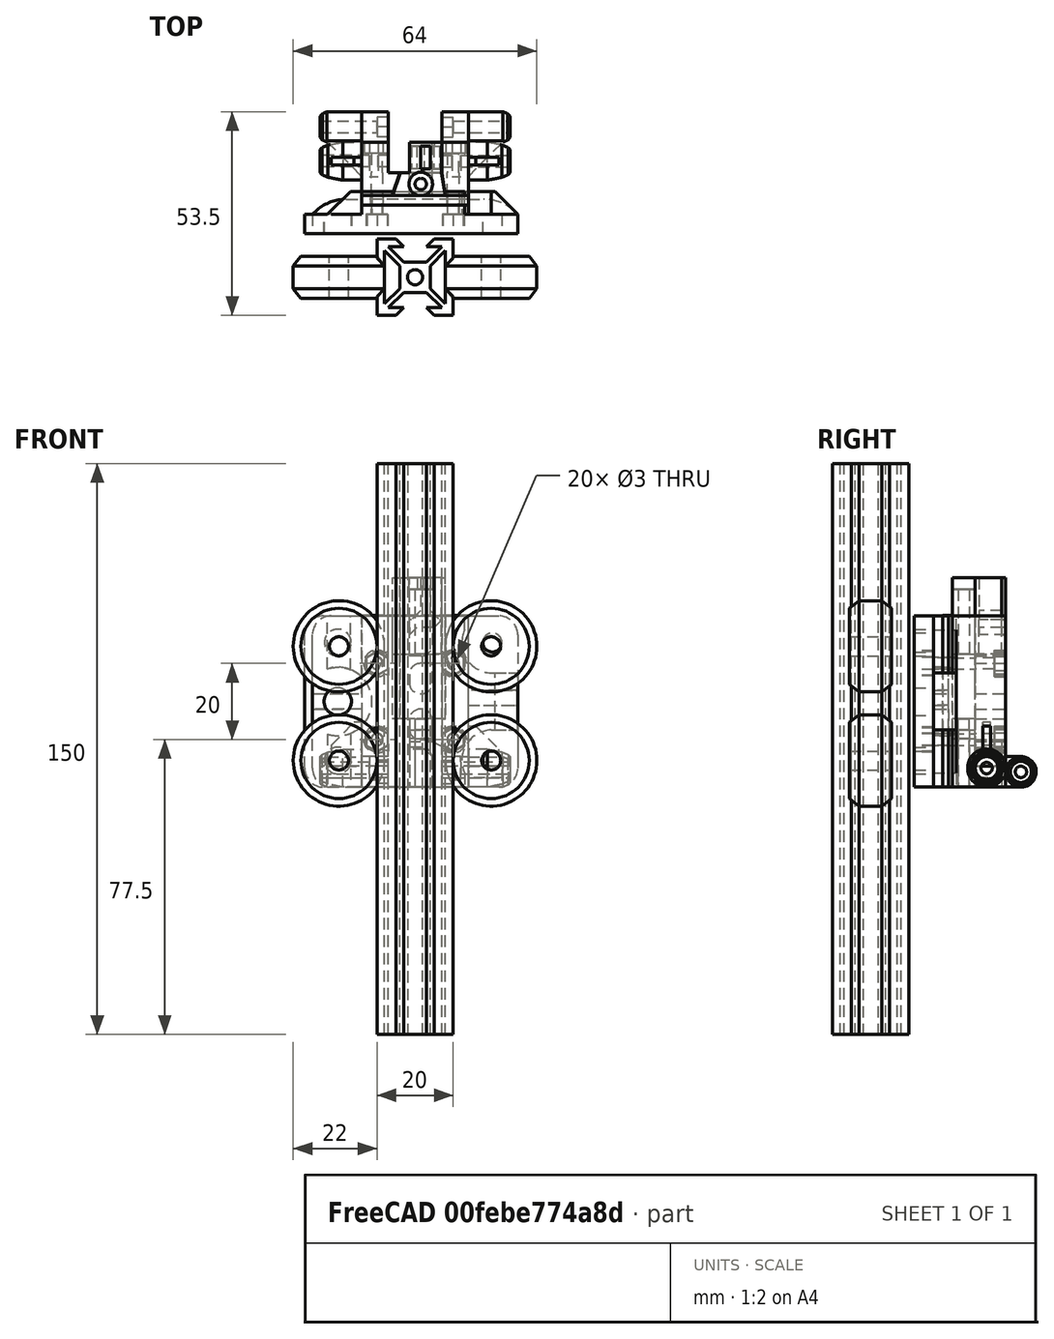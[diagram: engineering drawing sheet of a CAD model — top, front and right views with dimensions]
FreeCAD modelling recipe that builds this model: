
FCSTD DOCUMENT  (FreeCAD 0.18R16146 (Git))
Label: carriage
License: All rights reserved
LicenseURL: http://en.wikipedia.org/wiki/All_rights_reserved
objects: Sketcher::SketchObject×42, PartDesign::Pad×22, PartDesign::Pocket×16, PartDesign::Chamfer×13, PartDesign::Body×11, PartDesign::Fillet×5, PartDesign::Revolution×4, Mesh::Feature×3
note: 155 computed .brp shape members not serialized (recipe doc carries the construction recipe); baked Part::Feature solids carry a one-line shape summary decoded from their .brp

FEATURE [Sketcher::SketchObject] Sketch
  MapMode = 5
  Support = -> [XY_Plane]
  sketch-geometry (42):
    g0: LineSegment [constr] StartX=10 StartY=-10 StartZ=0 EndX=10 EndY=10 EndZ=0
    g1: LineSegment [constr] StartX=10 StartY=10 StartZ=0 EndX=-10 EndY=10 EndZ=0
    g2: LineSegment [constr] StartX=-10 StartY=10 StartZ=0 EndX=-10 EndY=-10 EndZ=0
    g3: LineSegment [constr] StartX=-10 StartY=-10 StartZ=0 EndX=10 EndY=-10 EndZ=0
    g4: Circle [constr] CenterX=0 CenterY=0 CenterZ=0 NormalX=0 NormalY=0 NormalZ=1 AngleXU=0 Radius=14.1421
    g5: Circle CenterX=0 CenterY=0 CenterZ=0 NormalX=0 NormalY=0 NormalZ=1 AngleXU=0 Radius=2
    g6: LineSegment StartX=-10 StartY=10 StartZ=0 EndX=-10 EndY=5 EndZ=0
    g7: LineSegment StartX=-10 StartY=10 StartZ=0 EndX=-5 EndY=10 EndZ=0
    g8: LineSegment StartX=10 StartY=10 StartZ=0 EndX=5 EndY=10 EndZ=0
    g9: LineSegment StartX=10 StartY=10 StartZ=0 EndX=10 EndY=5 EndZ=0
    g10: LineSegment StartX=10 StartY=-10 StartZ=0 EndX=10 EndY=-5 EndZ=0
    g11: LineSegment StartX=10 StartY=-10 StartZ=0 EndX=5 EndY=-10 EndZ=0
    g12: LineSegment StartX=-10 StartY=-10 StartZ=0 EndX=-5 EndY=-10 EndZ=0
    g13: LineSegment StartX=-10 StartY=-10 StartZ=0 EndX=-10 EndY=-5 EndZ=0
    g14: LineSegment StartX=-3 StartY=4 StartZ=0 EndX=3 EndY=4 EndZ=0
    g15: LineSegment StartX=4 StartY=3 StartZ=0 EndX=4 EndY=-3 EndZ=0
    g16: LineSegment StartX=-3 StartY=-4 StartZ=0 EndX=3 EndY=-4 EndZ=0
    g17: LineSegment StartX=-4 StartY=-3 StartZ=0 EndX=-4 EndY=3 EndZ=0
    g18: LineSegment StartX=-5 StartY=-10 StartZ=0 EndX=-3 EndY=-8 EndZ=0
    g19: LineSegment StartX=5 StartY=-10 StartZ=0 EndX=3 EndY=-8 EndZ=0
    g20: LineSegment StartX=-10 StartY=-5 StartZ=0 EndX=-8 EndY=-3 EndZ=0
    g21: LineSegment StartX=-10 StartY=5 StartZ=0 EndX=-8 EndY=3 EndZ=0
    g22: LineSegment StartX=-5 StartY=10 StartZ=0 EndX=-3.00001 EndY=7.99999 EndZ=0
    g23: LineSegment StartX=5 StartY=10 StartZ=0 EndX=2.99999 EndY=8.00001 EndZ=0
    g24: LineSegment StartX=10 StartY=-5 StartZ=0 EndX=7.99999 EndY=-3.00001 EndZ=0
    g25: LineSegment StartX=10 StartY=5 StartZ=0 EndX=8.00001 EndY=2.99999 EndZ=0
    g26: LineSegment StartX=-4 StartY=-3 StartZ=0 EndX=-8 EndY=-7 EndZ=0
    g27: LineSegment StartX=-3 StartY=-4 StartZ=0 EndX=-7 EndY=-8 EndZ=0
    g28: LineSegment StartX=3 StartY=-4 StartZ=0 EndX=6.99999 EndY=-8 EndZ=0
    g29: LineSegment StartX=4 StartY=-3 StartZ=0 EndX=7.99999 EndY=-7 EndZ=0
    g30: LineSegment StartX=-4 StartY=3 StartZ=0 EndX=-8 EndY=6.99999 EndZ=0
    g31: LineSegment StartX=-3 StartY=4 StartZ=0 EndX=-7 EndY=7.99999 EndZ=0
    g32: LineSegment StartX=3 StartY=4 StartZ=0 EndX=6.99998 EndY=8.00001 EndZ=0
    g33: LineSegment StartX=4 StartY=3 StartZ=0 EndX=8.00001 EndY=6.99999 EndZ=0
    g34: LineSegment StartX=-8 StartY=3 StartZ=0 EndX=-8 EndY=6.99999 EndZ=0
    g35: LineSegment StartX=-7 StartY=7.99999 StartZ=0 EndX=-3.00001 EndY=7.99999 EndZ=0
    g36: LineSegment StartX=2.99999 StartY=8.00001 StartZ=0 EndX=6.99998 EndY=8.00001 EndZ=0
    g37: LineSegment StartX=8.00001 StartY=6.99999 StartZ=0 EndX=8.00001 EndY=2.99999 EndZ=0
    g38: LineSegment StartX=7.99999 StartY=-7 StartZ=0 EndX=7.99999 EndY=-3.00001 EndZ=0
    g39: LineSegment StartX=3 StartY=-8 StartZ=0 EndX=6.99999 EndY=-8 EndZ=0
    g40: LineSegment StartX=-7 StartY=-8 StartZ=0 EndX=-3 EndY=-8 EndZ=0
    g41: LineSegment StartX=-8 StartY=-7 StartZ=0 EndX=-8 EndY=-3 EndZ=0
  constraints (118):
    c: Coincident(g0,g1)
    c: Coincident(g1,g2)
    c: Coincident(g2,g3)
    c: Coincident(g3,g0)
    c: Equal(g0,g1)
    c: Equal(g0,g2)
    c: Equal(g0,g3)
    c: PointOnObject(g0,g4)
    c: PointOnObject(g1,g4)
    c: PointOnObject(g2,g4)
    c: PointOnObject(g3,g4)
    c: Coincident(g4,g-1)
    c: DistanceX(g3,g3) = 20
    c: Horizontal(g1)
    c: Coincident(g5,g-1)
    c: Radius(g5) = 2
    c: Coincident(g6,g1)
    c: PointOnObject(g6,g2)
    c: Coincident(g7,g1)
    c: PointOnObject(g7,g1)
    c: Coincident(g8,g0)
    c: PointOnObject(g8,g1)
    c: Coincident(g9,g0)
    c: PointOnObject(g9,g0)
    c: Coincident(g10,g0)
    c: PointOnObject(g10,g0)
    c: Coincident(g11,g0)
    c: PointOnObject(g11,g3)
    c: Coincident(g12,g2)
    c: PointOnObject(g12,g3)
    c: Coincident(g13,g2)
    c: PointOnObject(g13,g2)
    c: Equal(g13,g12)
    c: Equal(g12,g11)
    c: Equal(g11,g10)
    c: Equal(g10,g9)
    c: Equal(g9,g8)
    c: Equal(g8,g7)
    c: Equal(g7,g6)
    c: DistanceX(g8,g8) = 5
    c: Horizontal(g14)
    c: Horizontal(g16)
    c: Equal(g15,g17)
    c: Equal(g16,g14)
    c: Equal(g14,g17)
    c: DistanceX(g14,g14) = 6
    c: Symmetric(g16,g16,g-2)
    c: Symmetric(g17,g17,g-1)
    c: Symmetric(g15,g15,g-1)
    c: Symmetric(g14,g14,g-2)
    c: Coincident(g18,g12)
    c: Coincident(g19,g11)
    c: Coincident(g20,g13)
    c: Coincident(g21,g6)
    c: Coincident(g22,g7)
    c: Coincident(g23,g8)
    c: Coincident(g24,g10)
    c: Coincident(g25,g9)
    c: Equal(g18,g19)
    c: Equal(g19,g24)
    c: Equal(g24,g20)
    c: Equal(g20,g21)
    c: Equal(g21,g22)
    c: Equal(g22,g23)
    c: Equal(g23,g25)
    c: DistanceX(g18,g19) = 6
    c: DistanceY(g20,g21) = 6
    c: DistanceX(g22,g23) = 6
    c: DistanceY(g24,g25) = 6
    c: Coincident(g26,g17)
    c: Coincident(g27,g16)
    c: Coincident(g28,g16)
    c: Coincident(g29,g15)
    c: Coincident(g30,g17)
    c: Coincident(g31,g14)
    c: Coincident(g33,g15)
    c: Coincident(g14,g32)
    c: Equal(g32,g33)
    c: Equal(g33,g30)
    c: Equal(g30,g31)
    c: Equal(g31,g26)
    c: Equal(g26,g27)
    c: Equal(g27,g28)
    c: Equal(g28,g29)
    c: Coincident(g34,g21)
    c: Coincident(g34,g30)
    c: Coincident(g35,g31)
    c: Coincident(g35,g22)
    c: Horizontal(g35)
    c: Coincident(g36,g23)
    c: Coincident(g36,g32)
    c: Coincident(g37,g33)
    c: Coincident(g37,g25)
    c: Coincident(g38,g29)
    c: Coincident(g38,g24)
    c: Coincident(g39,g19)
    c: Coincident(g39,g28)
    c: Coincident(g40,g27)
    c: Coincident(g40,g18)
    c: Coincident(g41,g26)
    c: Coincident(g41,g20)
    c: Equal(g41,g40)
    c: Equal(g40,g39)
    c: Equal(g39,g38)
    c: Equal(g38,g34)
    c: Equal(g34,g35)
    c: Equal(g35,g36)
    c: Equal(g36,g37)
    c: Vertical(g41)
    c: Vertical(g34)
    c: Vertical(g37)
    c: Vertical(g38)
    c: Horizontal(g39)
    c: Parallel(g28,g29)
    c: Parallel(g26,g27)
    c: Parallel(g30,g31)
    c: DistanceY(g-1,g14) = 4
    c: Angle(g24,g25) = 1.5708
FEATURE [PartDesign::Pad] Pad
  Length = 150
  Length2 = 100
  Profile = -> Sketch
  Type = 0
FEATURE [PartDesign::Body] Body  label="profile"
  Group = -> [Sketch,Pad]
  Origin = -> Origin
  Placement = pos=(0,0,-62) rot=(0,0,1;0rad)
  Tip = -> Pad
FEATURE [Sketcher::SketchObject] Sketch001
  MapMode = 5
  Support = -> [XY_Plane001]
  sketch-geometry (9):
    g0: LineSegment [constr] StartX=0 StartY=0 StartZ=0 EndX=2.5 EndY=0 EndZ=0
    g1: LineSegment [constr] StartX=0 StartY=0 StartZ=0 EndX=12 EndY=0 EndZ=0
    g2: LineSegment StartX=2.5 StartY=-5.5 StartZ=0 EndX=2.5 EndY=5.5 EndZ=0
    g3: LineSegment StartX=12 StartY=-3 StartZ=0 EndX=12 EndY=3 EndZ=0
    g4: LineSegment [constr] StartX=10 StartY=-5.5 StartZ=0 EndX=10 EndY=5.5 EndZ=0
    g5: LineSegment StartX=2.5 StartY=5.5 StartZ=0 EndX=10 EndY=5.5 EndZ=0
    g6: LineSegment StartX=10 StartY=5.5 StartZ=0 EndX=12 EndY=3 EndZ=0
    g7: LineSegment StartX=2.5 StartY=-5.5 StartZ=0 EndX=10 EndY=-5.5 EndZ=0
    g8: LineSegment StartX=10 StartY=-5.5 StartZ=0 EndX=12 EndY=-3 EndZ=0
  constraints (28):
    c: PointOnObject(g0,g-1)
    c: Horizontal(g0)
    c: Coincident(g0,g-1)
    c: DistanceX(g0,g0) = 2.5
    c: Coincident(g1,g-1)
    c: DistanceX(g1,g1) = 12
    c: Vertical(g2)
    c: Vertical(g3)
    c: Vertical(g4)
    c: PointOnObject(g0,g2)
    c: Symmetric(g2,g2,g1)
    c: Symmetric(g4,g4,g1)
    c: PointOnObject(g1,g3)
    c: Symmetric(g3,g3,g1)
    c: DistanceY(g3,g3) = 6
    c: DistanceY(g4,g4) = 11
    c: DistanceX(g4,g3) = 2
    c: DistanceY(g2,g2) = 11
    c: Coincident(g5,g2)
    c: Coincident(g5,g4)
    c: Horizontal(g5)
    c: Coincident(g6,g4)
    c: Coincident(g6,g3)
    c: Coincident(g7,g4)
    c: Horizontal(g7)
    c: Coincident(g8,g4)
    c: Coincident(g8,g3)
    c: Coincident(g2,g7)
FEATURE [PartDesign::Revolution] Revolution
  Angle = 360
  Axis = (0,1,0)
  Base = (0,0,0)
  Profile = -> Sketch001
  ReferenceAxis = -> Sketch001 [V_Axis]
  Reversed = true
FEATURE [PartDesign::Body] Body001  label="wheel"
  Group = -> [Sketch001,Revolution]
  Origin = -> Origin001
  Placement = pos=(20,0,10) rot=(0,0,1;0rad)
  Tip = -> Revolution
FEATURE [Sketcher::SketchObject] Sketch002
  MapMode = 5
  Support = -> [XY_Plane002]
  sketch-geometry (9):
    g0: LineSegment [constr] StartX=0 StartY=0 StartZ=0 EndX=2.5 EndY=0 EndZ=0
    g1: LineSegment [constr] StartX=0 StartY=0 StartZ=0 EndX=12 EndY=0 EndZ=0
    g2: LineSegment StartX=2.5 StartY=-5.5 StartZ=0 EndX=2.5 EndY=5.5 EndZ=0
    g3: LineSegment StartX=12 StartY=-3 StartZ=0 EndX=12 EndY=3 EndZ=0
    g4: LineSegment [constr] StartX=10 StartY=-5.5 StartZ=0 EndX=10 EndY=5.5 EndZ=0
    g5: LineSegment StartX=2.5 StartY=5.5 StartZ=0 EndX=10 EndY=5.5 EndZ=0
    g6: LineSegment StartX=10 StartY=5.5 StartZ=0 EndX=12 EndY=3 EndZ=0
    g7: LineSegment StartX=2.5 StartY=-5.5 StartZ=0 EndX=10 EndY=-5.5 EndZ=0
    g8: LineSegment StartX=10 StartY=-5.5 StartZ=0 EndX=12 EndY=-3 EndZ=0
  constraints (28):
    c: PointOnObject(g0,g-1)
    c: Horizontal(g0)
    c: Coincident(g0,g-1)
    c: DistanceX(g0,g0) = 2.5
    c: Coincident(g1,g-1)
    c: DistanceX(g1,g1) = 12
    c: Vertical(g2)
    c: Vertical(g3)
    c: Vertical(g4)
    c: PointOnObject(g0,g2)
    c: Symmetric(g2,g2,g1)
    c: Symmetric(g4,g4,g1)
    c: PointOnObject(g1,g3)
    c: Symmetric(g3,g3,g1)
    c: DistanceY(g3,g3) = 6
    c: DistanceY(g4,g4) = 11
    c: DistanceX(g4,g3) = 2
    c: DistanceY(g2,g2) = 11
    c: Coincident(g5,g2)
    c: Coincident(g5,g4)
    c: Horizontal(g5)
    c: Coincident(g6,g4)
    c: Coincident(g6,g3)
    c: Coincident(g7,g4)
    c: Horizontal(g7)
    c: Coincident(g8,g4)
    c: Coincident(g8,g3)
    c: Coincident(g2,g7)
FEATURE [PartDesign::Revolution] Revolution001
  Angle = 360
  Axis = (0,1,0)
  Base = (0,0,0)
  Profile = -> Sketch002
  ReferenceAxis = -> Sketch002 [V_Axis]
  Reversed = true
FEATURE [PartDesign::Body] Body002  label="wheel001"
  Group = -> [Sketch002,Revolution001]
  Origin = -> Origin002
  Placement = pos=(20,0,40) rot=(0,0,1;0rad)
  Tip = -> Revolution001
FEATURE [Sketcher::SketchObject] Sketch003
  MapMode = 5
  Support = -> [XY_Plane003]
  sketch-geometry (9):
    g0: LineSegment [constr] StartX=0 StartY=0 StartZ=0 EndX=2.5 EndY=0 EndZ=0
    g1: LineSegment [constr] StartX=0 StartY=0 StartZ=0 EndX=12 EndY=0 EndZ=0
    g2: LineSegment StartX=2.5 StartY=-5.5 StartZ=0 EndX=2.5 EndY=5.5 EndZ=0
    g3: LineSegment StartX=12 StartY=-3 StartZ=0 EndX=12 EndY=3 EndZ=0
    g4: LineSegment [constr] StartX=10 StartY=-5.5 StartZ=0 EndX=10 EndY=5.5 EndZ=0
    g5: LineSegment StartX=2.5 StartY=5.5 StartZ=0 EndX=10 EndY=5.5 EndZ=0
    g6: LineSegment StartX=10 StartY=5.5 StartZ=0 EndX=12 EndY=3 EndZ=0
    g7: LineSegment StartX=2.5 StartY=-5.5 StartZ=0 EndX=10 EndY=-5.5 EndZ=0
    g8: LineSegment StartX=10 StartY=-5.5 StartZ=0 EndX=12 EndY=-3 EndZ=0
  constraints (28):
    c: PointOnObject(g0,g-1)
    c: Horizontal(g0)
    c: Coincident(g0,g-1)
    c: DistanceX(g0,g0) = 2.5
    c: Coincident(g1,g-1)
    c: DistanceX(g1,g1) = 12
    c: Vertical(g2)
    c: Vertical(g3)
    c: Vertical(g4)
    c: PointOnObject(g0,g2)
    c: Symmetric(g2,g2,g1)
    c: Symmetric(g4,g4,g1)
    c: PointOnObject(g1,g3)
    c: Symmetric(g3,g3,g1)
    c: DistanceY(g3,g3) = 6
    c: DistanceY(g4,g4) = 11
    c: DistanceX(g4,g3) = 2
    c: DistanceY(g2,g2) = 11
    c: Coincident(g5,g2)
    c: Coincident(g5,g4)
    c: Horizontal(g5)
    c: Coincident(g6,g4)
    c: Coincident(g6,g3)
    c: Coincident(g7,g4)
    c: Horizontal(g7)
    c: Coincident(g8,g4)
    c: Coincident(g8,g3)
    c: Coincident(g2,g7)
FEATURE [PartDesign::Revolution] Revolution002
  Angle = 360
  Axis = (0,1,0)
  Base = (0,0,0)
  Profile = -> Sketch003
  ReferenceAxis = -> Sketch003 [V_Axis]
  Reversed = true
FEATURE [PartDesign::Body] Body003  label="wheel002"
  Group = -> [Sketch003,Revolution002]
  Origin = -> Origin003
  Placement = pos=(-20,0,10) rot=(0,0,1;0rad)
  Tip = -> Revolution002
FEATURE [Sketcher::SketchObject] Sketch004
  MapMode = 5
  Support = -> [XY_Plane004]
  sketch-geometry (9):
    g0: LineSegment [constr] StartX=0 StartY=0 StartZ=0 EndX=2.5 EndY=0 EndZ=0
    g1: LineSegment [constr] StartX=0 StartY=0 StartZ=0 EndX=12 EndY=0 EndZ=0
    g2: LineSegment StartX=2.5 StartY=-5.5 StartZ=0 EndX=2.5 EndY=5.5 EndZ=0
    g3: LineSegment StartX=12 StartY=-3 StartZ=0 EndX=12 EndY=3 EndZ=0
    g4: LineSegment [constr] StartX=10 StartY=-5.5 StartZ=0 EndX=10 EndY=5.5 EndZ=0
    g5: LineSegment StartX=2.5 StartY=5.5 StartZ=0 EndX=10 EndY=5.5 EndZ=0
    g6: LineSegment StartX=10 StartY=5.5 StartZ=0 EndX=12 EndY=3 EndZ=0
    g7: LineSegment StartX=2.5 StartY=-5.5 StartZ=0 EndX=10 EndY=-5.5 EndZ=0
    g8: LineSegment StartX=10 StartY=-5.5 StartZ=0 EndX=12 EndY=-3 EndZ=0
  constraints (28):
    c: PointOnObject(g0,g-1)
    c: Horizontal(g0)
    c: Coincident(g0,g-1)
    c: DistanceX(g0,g0) = 2.5
    c: Coincident(g1,g-1)
    c: DistanceX(g1,g1) = 12
    c: Vertical(g2)
    c: Vertical(g3)
    c: Vertical(g4)
    c: PointOnObject(g0,g2)
    c: Symmetric(g2,g2,g1)
    c: Symmetric(g4,g4,g1)
    c: PointOnObject(g1,g3)
    c: Symmetric(g3,g3,g1)
    c: DistanceY(g3,g3) = 6
    c: DistanceY(g4,g4) = 11
    c: DistanceX(g4,g3) = 2
    c: DistanceY(g2,g2) = 11
    c: Coincident(g5,g2)
    c: Coincident(g5,g4)
    c: Horizontal(g5)
    c: Coincident(g6,g4)
    c: Coincident(g6,g3)
    c: Coincident(g7,g4)
    c: Horizontal(g7)
    c: Coincident(g8,g4)
    c: Coincident(g8,g3)
    c: Coincident(g2,g7)
FEATURE [PartDesign::Revolution] Revolution003
  Angle = 360
  Axis = (0,1,0)
  Base = (0,0,0)
  Profile = -> Sketch004
  ReferenceAxis = -> Sketch004 [V_Axis]
  Reversed = true
FEATURE [PartDesign::Body] Body004  label="wheel003"
  Group = -> [Sketch004,Revolution003]
  Origin = -> Origin004
  Placement = pos=(-20,0,40) rot=(0,0,1;0rad)
  Tip = -> Revolution003
FEATURE [Sketcher::SketchObject] Sketch005
  MapMode = 5
  Placement = pos=(0,0,0) rot=(1,0,0;1.5708rad)
  Support = -> [XZ_Plane005]
  sketch-geometry (8):
    g0: LineSegment StartX=-27 StartY=48 StartZ=0 EndX=27 EndY=48 EndZ=0
    g1: LineSegment StartX=27 StartY=48 StartZ=0 EndX=27 EndY=3 EndZ=0
    g2: LineSegment StartX=27 StartY=3 StartZ=0 EndX=-27 EndY=3 EndZ=0
    g3: LineSegment StartX=-27 StartY=3 StartZ=0 EndX=-27 EndY=48 EndZ=0
    g4: Circle CenterX=-20.3 CenterY=41 CenterZ=0 NormalX=0 NormalY=0 NormalZ=1 AngleXU=0 Radius=3.5
    g5: Circle CenterX=-20.3 CenterY=10 CenterZ=0 NormalX=0 NormalY=0 NormalZ=1 AngleXU=0 Radius=3.5
    g6: Circle CenterX=20.3 CenterY=10 CenterZ=0 NormalX=0 NormalY=0 NormalZ=1 AngleXU=0 Radius=2.5
    g7: Circle CenterX=20.3 CenterY=41 CenterZ=0 NormalX=0 NormalY=0 NormalZ=1 AngleXU=0 Radius=2.5
  constraints (24):
    c: Coincident(g0,g1)
    c: Coincident(g1,g2)
    c: Coincident(g2,g3)
    c: Coincident(g3,g0)
    c: Horizontal(g0)
    c: Horizontal(g2)
    c: Vertical(g1)
    c: Vertical(g3)
    c: DistanceX(g2,g2) = 54
    c: DistanceY(g1,g1) = 45
    c: Symmetric(g1,g2,g-2)
    c: Radius(g7) = 2.5
    c: Equal(g7,g6)
    c: Radius(g5) = 3.5
    c: Equal(g5,g4)
    c: DistanceX(g7,g0) = 6.7
    c: DistanceY(g7,g0) = 7
    c: DistanceY(g1,g6) = 7
    c: DistanceX(g6,g1) = 6.7
    c: DistanceX(g2,g5) = 6.7
    c: DistanceX(g0,g4) = 6.7
    c: DistanceY(g4,g0) = 7
    c: DistanceY(g2,g5) = 7
    c: DistanceY(g-1,g1) = 3
FEATURE [PartDesign::Pad] Pad001
  Length = 5
  Length2 = 100
  Placement = pos=(0,0,0) rot=(1,0,0;1.5708rad)
  Profile = -> Sketch005
  Type = 0
FEATURE [PartDesign::Fillet] Fillet
  Base = -> Pad001 [Edge1,Edge8,Edge2,Edge5]
  BaseFeature = -> Pad001
  Placement = pos=(0,0,0) rot=(1,0,0;1.5708rad)
  Radius = 5
FEATURE [Sketcher::SketchObject] Sketch006
  ExternalGeometry = -> [Fillet]
  MapMode = 5
  Placement = pos=(0,-1e-16,0) rot=(-1,0,0;1.5708rad)
  Support = -> [Fillet]
  sketch-geometry (33):
    g0: LineSegment [constr] StartX=-10 StartY=-15.5 StartZ=0 EndX=10 EndY=-15.5 EndZ=0
    g1: LineSegment [constr] StartX=10 StartY=-15.5 StartZ=0 EndX=10 EndY=-35.5 EndZ=0
    g2: LineSegment [constr] StartX=10.7745 StartY=-35.5 StartZ=0 EndX=-10 EndY=-35.5 EndZ=0
    g3: LineSegment [constr] StartX=-10 StartY=-35.5 StartZ=0 EndX=-10 EndY=-15.5 EndZ=0
    g4: LineSegment StartX=-7.31532 StartY=-17.05 StartZ=0 EndX=-7.31532 EndY=-13.95 EndZ=0
    g5: LineSegment StartX=-7.31532 StartY=-13.95 StartZ=0 EndX=-10 EndY=-12.4 EndZ=0
    g6: LineSegment StartX=-10 StartY=-12.4 StartZ=0 EndX=-12.6847 EndY=-13.95 EndZ=0
    g7: LineSegment StartX=-12.6847 StartY=-13.95 StartZ=0 EndX=-12.6847 EndY=-17.05 EndZ=0
    g8: LineSegment StartX=-12.6847 StartY=-17.05 StartZ=0 EndX=-10 EndY=-18.6 EndZ=0
    g9: LineSegment StartX=-10 StartY=-18.6 StartZ=0 EndX=-7.31532 EndY=-17.05 EndZ=0
    g10: Circle [constr] CenterX=-10 CenterY=-15.5 CenterZ=0 NormalX=0 NormalY=0 NormalZ=1 AngleXU=0 Radius=3.1
    g11: LineSegment StartX=-7.31532 StartY=-33.95 StartZ=0 EndX=-10 EndY=-32.4 EndZ=0
    g12: LineSegment StartX=-10 StartY=-32.4 StartZ=0 EndX=-12.6847 EndY=-33.95 EndZ=0
    g13: LineSegment StartX=-12.6847 StartY=-33.95 StartZ=0 EndX=-12.6847 EndY=-37.05 EndZ=0
    g14: LineSegment StartX=-12.6847 StartY=-37.05 StartZ=0 EndX=-10 EndY=-38.6 EndZ=0
    g15: LineSegment StartX=-10 StartY=-38.6 StartZ=0 EndX=-7.31532 EndY=-37.05 EndZ=0
    g16: LineSegment StartX=-7.31532 StartY=-37.05 StartZ=0 EndX=-7.31532 EndY=-33.95 EndZ=0
    g17: Circle [constr] CenterX=-10 CenterY=-35.5 CenterZ=0 NormalX=0 NormalY=0 NormalZ=1 AngleXU=0 Radius=3.1
    g18: LineSegment StartX=12.6847 StartY=-37.05 StartZ=0 EndX=12.6847 EndY=-33.95 EndZ=0
    g19: LineSegment StartX=12.6847 StartY=-33.95 StartZ=0 EndX=10 EndY=-32.4 EndZ=0
    g20: LineSegment StartX=10 StartY=-32.4 StartZ=0 EndX=7.31532 EndY=-33.95 EndZ=0
    g21: LineSegment StartX=7.31532 StartY=-33.95 StartZ=0 EndX=7.31532 EndY=-37.05 EndZ=0
    g22: LineSegment StartX=7.31532 StartY=-37.05 StartZ=0 EndX=10 EndY=-38.6 EndZ=0
    g23: LineSegment StartX=10 StartY=-38.6 StartZ=0 EndX=12.6847 EndY=-37.05 EndZ=0
    g24: Circle [constr] CenterX=10 CenterY=-35.5 CenterZ=0 NormalX=0 NormalY=0 NormalZ=1 AngleXU=0 Radius=3.1
    g25: LineSegment StartX=12.6847 StartY=-17.05 StartZ=0 EndX=12.6847 EndY=-13.95 EndZ=0
    g26: LineSegment StartX=12.6847 StartY=-13.95 StartZ=0 EndX=10 EndY=-12.4 EndZ=0
    g27: LineSegment StartX=10 StartY=-12.4 StartZ=0 EndX=7.31532 EndY=-13.95 EndZ=0
    g28: LineSegment StartX=7.31532 StartY=-13.95 StartZ=0 EndX=7.31532 EndY=-17.05 EndZ=0
    g29: LineSegment StartX=7.31532 StartY=-17.05 StartZ=0 EndX=10 EndY=-18.6 EndZ=0
    g30: LineSegment StartX=10 StartY=-18.6 StartZ=0 EndX=12.6847 EndY=-17.05 EndZ=0
    g31: Circle [constr] CenterX=10 CenterY=-15.5 CenterZ=0 NormalX=0 NormalY=0 NormalZ=1 AngleXU=0 Radius=3.1
    g32: LineSegment [constr] StartX=27 StartY=-25.5 StartZ=0 EndX=10 EndY=-25.5 EndZ=0
  constraints (78):
    c: Coincident(g0,g1)
    c: Coincident(g2,g3)
    c: Coincident(g3,g0)
    c: Horizontal(g0)
    c: Horizontal(g2)
    c: Vertical(g1)
    c: Vertical(g3)
    c: DistanceX(g0,g0) = 20
    c: DistanceY(g1,g1) = 20
    c: Symmetric(g2,g1,g-2)
    c: Coincident(g4,g5)
    c: Coincident(g5,g6)
    c: Coincident(g6,g7)
    c: Coincident(g7,g8)
    c: Coincident(g8,g9)
    c: Coincident(g9,g4)
    c: Equal(g4, g5-g9) x5
    c: PointOnObject(g4,g10)
    c: PointOnObject(g5,g10)
    c: PointOnObject(g6,g10)
    c: PointOnObject(g7,g10)
    c: PointOnObject(g8,g10)
    c: PointOnObject(g9,g10)
    c: Coincident(g10,g0)
    c: Coincident(g11,g12)
    c: Coincident(g12,g13)
    c: Coincident(g13,g14)
    c: Coincident(g14,g15)
    c: Coincident(g15,g16)
    c: Coincident(g16,g11)
    c: Equal(g11, g12-g16) x5
    c: PointOnObject(g11,g17)
    c: PointOnObject(g12,g17)
    c: PointOnObject(g13,g17)
    c: PointOnObject(g14,g17)
    c: PointOnObject(g15,g17)
    c: PointOnObject(g16,g17)
    c: Coincident(g17,g2)
    c: Coincident(g18,g19)
    c: Coincident(g19,g20)
    c: Coincident(g20,g21)
    c: Coincident(g21,g22)
    c: Coincident(g22,g23)
    c: Coincident(g23,g18)
    c: Equal(g18, g19-g23) x5
    c: PointOnObject(g18,g24)
    c: PointOnObject(g19,g24)
    c: PointOnObject(g20,g24)
    c: PointOnObject(g21,g24)
    c: PointOnObject(g22,g24)
    c: PointOnObject(g23,g24)
    c: Coincident(g25,g26)
    c: Coincident(g26,g27)
    c: Coincident(g27,g28)
    c: Coincident(g28,g29)
    c: Coincident(g29,g30)
    c: Coincident(g30,g25)
    c: Equal(g25, g26-g30) x5
    c: PointOnObject(g25,g31)
    c: PointOnObject(g26,g31)
    c: PointOnObject(g27,g31)
    c: PointOnObject(g28,g31)
    c: PointOnObject(g29,g31)
    c: PointOnObject(g30,g31)
    c: Coincident(g31,g0)
    c: Vertical(g7)
    c: Vertical(g13)
    c: Vertical(g28)
    c: Vertical(g21)
    c: Radius(g31) = 3.1
    c: Equal(g31,g10)
    c: Equal(g31,g17)
    c: Equal(g31,g24)
    c: PointOnObject(g32,g-3)
    c: PointOnObject(g32,g1)
    c: Symmetric(g-3,g-3,g32)
    c: Coincident(g24,g1)
    c: Symmetric(g1,g0,g32)
FEATURE [PartDesign::Pocket] Pocket
  BaseFeature = -> Fillet
  Length = 5
  Length2 = 100
  Placement = pos=(0,0,0) rot=(1,0,0;1.5708rad)
  Profile = -> Sketch006
  Type = 0
FEATURE [Mesh::Feature] bottom_bracket
  Placement = pos=(35,-15,92) rot=(0,1,0;3.14159rad)
FEATURE [Sketcher::SketchObject] Sketch007
  ExternalGeometry = -> [Pocket]
  MapMode = 5
  Placement = pos=(0,-1e-16,0) rot=(-1,0,0;1.5708rad)
  Support = -> [Pocket]
  sketch-geometry (21):
    g0: LineSegment StartX=-14 StartY=-3 StartZ=0 EndX=14 EndY=-3 EndZ=0
    g1: LineSegment StartX=14 StartY=-3 StartZ=0 EndX=14 EndY=-24.5 EndZ=0
    g2: LineSegment StartX=14 StartY=-48 StartZ=0 EndX=-14 EndY=-48 EndZ=0
    g3: LineSegment StartX=-14 StartY=-23.5 StartZ=0 EndX=-14 EndY=-3 EndZ=0
    g4: LineSegment [constr] StartX=-10 StartY=-15.5 StartZ=0 EndX=10 EndY=-15.5 EndZ=0
    g5: LineSegment [constr] StartX=10 StartY=-15.5 StartZ=0 EndX=10 EndY=-35.5 EndZ=0
    g6: LineSegment [constr] StartX=10 StartY=-35.5 StartZ=0 EndX=-10 EndY=-35.5 EndZ=0
    g7: LineSegment [constr] StartX=-10 StartY=-35.5 StartZ=0 EndX=-10 EndY=-15.5 EndZ=0
    g8: Circle CenterX=-10 CenterY=-15.5 CenterZ=0 NormalX=0 NormalY=0 NormalZ=1 AngleXU=0 Radius=1.5
    g9: Circle CenterX=10 CenterY=-15.5 CenterZ=0 NormalX=0 NormalY=0 NormalZ=1 AngleXU=0 Radius=1.5
    g10: Circle CenterX=-10 CenterY=-35.5 CenterZ=0 NormalX=0 NormalY=0 NormalZ=1 AngleXU=0 Radius=1.5
    g11: Circle CenterX=10 CenterY=-35.5 CenterZ=0 NormalX=0 NormalY=0 NormalZ=1 AngleXU=0 Radius=1.5
    g12: LineSegment StartX=-14 StartY=-23.5 StartZ=0 EndX=-27 EndY=-23.5 EndZ=0
    g13: LineSegment StartX=-27 StartY=-23.5 StartZ=0 EndX=-27 EndY=-27.5 EndZ=0
    g14: LineSegment StartX=-27 StartY=-27.5 StartZ=0 EndX=-14 EndY=-27.5 EndZ=0
    g15: LineSegment StartX=-14 StartY=-27.5 StartZ=0 EndX=-14 EndY=-48 EndZ=0
    g16: LineSegment StartX=14 StartY=-24.5 StartZ=0 EndX=27 EndY=-24.5 EndZ=0
    g17: LineSegment StartX=27 StartY=-24.5 StartZ=0 EndX=27 EndY=-28.5 EndZ=0
    g18: LineSegment StartX=27 StartY=-28.5 StartZ=0 EndX=14 EndY=-28.5 EndZ=0
    g19: LineSegment StartX=14 StartY=-28.5 StartZ=0 EndX=14 EndY=-48 EndZ=0
    g20: LineSegment [constr] StartX=-14 StartY=-27.5 StartZ=0 EndX=-14 EndY=-23.5 EndZ=0
  constraints (58):
    c: Coincident(g0,g1)
    c: Coincident(g3,g0)
    c: Horizontal(g0)
    c: Horizontal(g2)
    c: Vertical(g1)
    c: Vertical(g3)
    c: PointOnObject(g0,g-3)
    c: DistanceX(g0,g0) = 28
    c: Symmetric(g0,g0,g-2)
    c: Coincident(g4,g5)
    c: Coincident(g5,g6)
    c: Coincident(g6,g7)
    c: Coincident(g7,g4)
    c: Horizontal(g4)
    c: Horizontal(g6)
    c: Vertical(g5)
    c: Vertical(g7)
    c: DistanceY(g4,g0) = 12.5
    c: Symmetric(g6,g5,g-2)
    c: DistanceX(g4,g4) = 20
    c: DistanceY(g5,g5) = 20
    c: Coincident(g8,g4)
    c: Coincident(g9,g4)
    c: Coincident(g10,g6)
    c: Coincident(g11,g5)
    c: Radius(g11) = 1.5
    c: Equal(g11,g10)
    c: Equal(g11,g8)
    c: Equal(g11,g9)
    c: Coincident(g12,g3)
    c: Horizontal(g12)
    c: Coincident(g13,g12)
    c: Coincident(g14,g13)
    c: Horizontal(g14)
    c: Coincident(g15,g14)
    c: Coincident(g15,g2)
    c: Vertical(g15)
    c: Vertical(g13)
    c: Coincident(g16,g1)
    c: Horizontal(g16)
    c: Coincident(g17,g16)
    c: Vertical(g17)
    c: Coincident(g18,g17)
    c: Horizontal(g18)
    c: Coincident(g19,g18)
    c: Coincident(g19,g2)
    c: Vertical(g19)
    c: PointOnObject(g2,g-4)
    c: PointOnObject(g13,g-6)
    c: PointOnObject(g17,g-5)
    c: Equal(g17,g13)
    c: Equal(g2,g0)
    c: Coincident(g20,g14)
    c: Coincident(g20,g3)
    c: Vertical(g20)
    c: DistanceY(g3,g4) = 8
    c: DistanceY(g1,g4) = 9
    c: DistanceY(g13,g13) = 4
FEATURE [PartDesign::Pad] Pad002
  BaseFeature = -> Pocket
  Length = 4
  Length2 = 100
  Placement = pos=(0,0,0) rot=(1,0,0;1.5708rad)
  Profile = -> Sketch007
  Type = 0
FEATURE [Mesh::Feature] carriage_tensioner_52
  Placement = pos=(51,20.5,20) rot=(1,0,0;4.71239rad)
FEATURE [PartDesign::Chamfer] Chamfer
  Base = -> Pad002 [Edge136,Edge72]
  BaseFeature = -> Pad002
  Placement = pos=(0,0,0) rot=(1,0,0;1.5708rad)
  Size = 3.99
FEATURE [PartDesign::Fillet] Fillet001
  Base = -> Chamfer [Edge17,Edge10]
  BaseFeature = -> Chamfer
  Placement = pos=(0,0,0) rot=(1,0,0;1.5708rad)
  Radius = 12
FEATURE [PartDesign::Body] Body005  label="carriage"
  Group = -> [Sketch005,Pad001,Fillet,Sketch006,Pocket,Sketch007,Pad002,Chamfer,Fillet001]
  Origin = -> Origin005
  Placement = pos=(0,16.5,0) rot=(0,0,1;0rad)
  Tip = -> Fillet001
FEATURE [Mesh::Feature] top_bracket
  Placement = pos=(-35,-15,-42) rot=(0,0,1;0rad)
FEATURE [Sketcher::SketchObject] Sketch008
  MapMode = 5
  Placement = pos=(0,0,0) rot=(1,0,0;1.5708rad)
  Support = -> [XZ_Plane006]
  sketch-geometry (20):
    g0: LineSegment StartX=0 StartY=0 StartZ=0 EndX=28 EndY=0 EndZ=0
    g1: LineSegment StartX=28 StartY=0 StartZ=0 EndX=28 EndY=45 EndZ=0
    g2: LineSegment StartX=28 StartY=45 StartZ=0 EndX=0 EndY=45 EndZ=0
    g3: LineSegment StartX=0 StartY=45 StartZ=0 EndX=0 EndY=0 EndZ=0
    g4: LineSegment [constr] StartX=4 StartY=32.5 StartZ=0 EndX=24 EndY=32.5 EndZ=0
    g5: LineSegment [constr] StartX=24 StartY=32.5 StartZ=0 EndX=24 EndY=12.5 EndZ=0
    g6: LineSegment [constr] StartX=24 StartY=12.5 StartZ=0 EndX=4 EndY=12.5 EndZ=0
    g7: LineSegment [constr] StartX=4 StartY=12.5 StartZ=0 EndX=4 EndY=32.5 EndZ=0
    g8: LineSegment [constr] StartX=0 StartY=22.5 StartZ=0 EndX=4 EndY=22.5 EndZ=0
    g9: LineSegment [constr] StartX=14 StartY=45 StartZ=0 EndX=14 EndY=32.5 EndZ=0
    g10: Circle CenterX=4 CenterY=32.5 CenterZ=0 NormalX=0 NormalY=0 NormalZ=1 AngleXU=0 Radius=1.5
    g11: Circle CenterX=24 CenterY=32.5 CenterZ=0 NormalX=0 NormalY=0 NormalZ=1 AngleXU=0 Radius=1.5
    g12: Circle CenterX=4 CenterY=12.5 CenterZ=0 NormalX=0 NormalY=0 NormalZ=1 AngleXU=0 Radius=1.5
    g13: Circle CenterX=24 CenterY=12.5 CenterZ=0 NormalX=0 NormalY=0 NormalZ=1 AngleXU=0 Radius=1.5
    g14: LineSegment [constr] StartX=0 StartY=45 StartZ=0 EndX=-12 EndY=25.5 EndZ=0
    g15: LineSegment [constr] StartX=-12 StartY=25.5 StartZ=0 EndX=-12 EndY=19.5 EndZ=0
    g16: LineSegment [constr] StartX=-12 StartY=19.5 StartZ=0 EndX=0 EndY=0 EndZ=0
    g17: LineSegment [constr] StartX=28 StartY=0 StartZ=0 EndX=40 EndY=19.5 EndZ=0
    g18: LineSegment [constr] StartX=40 StartY=19.5 StartZ=0 EndX=40 EndY=25.5 EndZ=0
    g19: LineSegment [constr] StartX=40 StartY=25.5 StartZ=0 EndX=28 EndY=45 EndZ=0
  constraints (54):
    c: Coincident(g0,g1)
    c: Coincident(g1,g2)
    c: Coincident(g2,g3)
    c: Coincident(g3,g0)
    c: Horizontal(g0)
    c: Horizontal(g2)
    c: Vertical(g1)
    c: Vertical(g3)
    c: PointOnObject(g0,g-1)
    c: Coincident(g0,g-1)
    c: DistanceX(g0,g0) = 28
    c: DistanceY(g1,g1) = 45
    c: Coincident(g4,g5)
    c: Coincident(g5,g6)
    c: Coincident(g6,g7)
    c: Coincident(g7,g4)
    c: Horizontal(g6)
    c: Vertical(g5)
    c: Vertical(g7)
    c: PointOnObject(g8,g3)
    c: PointOnObject(g8,g7)
    c: Symmetric(g6,g4,g8)
    c: Symmetric(g-1,g2,g8)
    c: PointOnObject(g9,g2)
    c: PointOnObject(g9,g4)
    c: Vertical(g9)
    c: Symmetric(g4,g4,g9)
    c: Symmetric(g1,g2,g9)
    c: DistanceX(g4,g4) = 20
    c: DistanceY(g5,g5) = 20
    c: Coincident(g10,g4)
    c: Coincident(g11,g4)
    c: Coincident(g12,g6)
    c: Coincident(g13,g5)
    c: Radius(g13) = 1.5
    c: Equal(g13,g11)
    c: Equal(g13,g10)
    c: Equal(g13,g12)
    c: Coincident(g14,g2)
    c: Coincident(g15,g14)
    c: Vertical(g15)
    c: Coincident(g16,g15)
    c: Coincident(g16,g-1)
    c: Coincident(g17,g0)
    c: Coincident(g18,g17)
    c: Vertical(g18)
    c: Coincident(g19,g18)
    c: Coincident(g19,g1)
    c: Equal(g18,g15)
    c: Equal(g19,g14)
    c: Equal(g16,g17)
    c: DistanceY(g15,g15) = 6
    c: Equal(g16,g14)
    c: DistanceX(g14,g18) = 52
FEATURE [PartDesign::Pad] Pad003
  Length = 6
  Length2 = 100
  Placement = pos=(0,0,0) rot=(1,0,0;1.5708rad)
  Profile = -> Sketch008
  Type = 0
FEATURE [Sketcher::SketchObject] Sketch009
  ExternalGeometry = -> [Pad003]
  MapMode = 5
  Placement = pos=(0,-1e-16,0) rot=(-1,0,0;1.5708rad)
  Support = -> [Pad003]
  sketch-geometry (32):
    g0: LineSegment StartX=0 StartY=0 StartZ=0 EndX=7 EndY=0 EndZ=0
    g1: LineSegment StartX=7 StartY=0 StartZ=0 EndX=7 EndY=-45 EndZ=0
    g2: LineSegment StartX=7 StartY=-45 StartZ=0 EndX=0 EndY=-45 EndZ=0
    g3: LineSegment StartX=0 StartY=-45 StartZ=0 EndX=0 EndY=0 EndZ=0
    g4: LineSegment StartX=21 StartY=0 StartZ=0 EndX=28 EndY=0 EndZ=0
    g5: LineSegment StartX=28 StartY=0 StartZ=0 EndX=28 EndY=-45 EndZ=0
    g6: LineSegment StartX=28 StartY=-45 StartZ=0 EndX=21 EndY=-45 EndZ=0
    g7: LineSegment StartX=21 StartY=-45 StartZ=0 EndX=21 EndY=0 EndZ=0
    g8: LineSegment StartX=12.5 StartY=0 StartZ=0 EndX=18.5 EndY=0 EndZ=0
    g9: LineSegment StartX=18.5 StartY=0 StartZ=0 EndX=18.5 EndY=-10.5 EndZ=0
    g10: LineSegment StartX=18.5 StartY=-10.5 StartZ=0 EndX=12.5 EndY=-10.5 EndZ=0
    g11: LineSegment StartX=12.5 StartY=-10.5 StartZ=0 EndX=12.5 EndY=0 EndZ=0
    g12: LineSegment StartX=12.5 StartY=-12.5 StartZ=0 EndX=18.5 EndY=-12.5 EndZ=0
    g13: LineSegment StartX=18.5 StartY=-12.5 StartZ=0 EndX=18.5 EndY=-20.5 EndZ=0
    g14: LineSegment StartX=18.5 StartY=-20.5 StartZ=0 EndX=12.5 EndY=-20.5 EndZ=0
    g15: LineSegment StartX=12.5 StartY=-20.5 StartZ=0 EndX=12.5 EndY=-12.5 EndZ=0
    g16: LineSegment [constr] StartX=14 StartY=0 StartZ=0 EndX=14 EndY=-45 EndZ=0
    g17: Circle CenterX=24 CenterY=-12.5 CenterZ=0 NormalX=0 NormalY=0 NormalZ=1 AngleXU=0 Radius=1.5
    g18: Circle CenterX=4 CenterY=-12.5 CenterZ=0 NormalX=0 NormalY=0 NormalZ=1 AngleXU=0 Radius=1.5
    g19: Circle CenterX=4 CenterY=-32.5 CenterZ=0 NormalX=0 NormalY=0 NormalZ=1 AngleXU=0 Radius=1.5
    g20: Circle CenterX=24 CenterY=-32.5 CenterZ=0 NormalX=0 NormalY=0 NormalZ=1 AngleXU=0 Radius=1.5
    g21: LineSegment [constr] StartX=12.5 StartY=-12.5 StartZ=0 EndX=12.5 EndY=-10.5 EndZ=0
    g22: LineSegment StartX=12.5 StartY=-24.5 StartZ=0 EndX=18.5 EndY=-24.5 EndZ=0
    g23: LineSegment StartX=18.5 StartY=-24.5 StartZ=0 EndX=18.5 EndY=-32.5 EndZ=0
    g24: LineSegment StartX=18.5 StartY=-32.5 StartZ=0 EndX=12.5 EndY=-32.5 EndZ=0
    g25: LineSegment StartX=12.5 StartY=-32.5 StartZ=0 EndX=12.5 EndY=-24.5 EndZ=0
    g26: LineSegment StartX=12.5 StartY=-45 StartZ=0 EndX=18.5 EndY=-45 EndZ=0
    g27: LineSegment StartX=18.5 StartY=-45 StartZ=0 EndX=18.5 EndY=-34.5 EndZ=0
    g28: LineSegment StartX=18.5 StartY=-34.5 StartZ=0 EndX=12.5 EndY=-34.5 EndZ=0
    g29: LineSegment StartX=12.5 StartY=-34.5 StartZ=0 EndX=12.5 EndY=-45 EndZ=0
    g30: LineSegment [constr] StartX=12.5 StartY=-20.5 StartZ=0 EndX=12.5 EndY=-24.5 EndZ=0
    g31: LineSegment [constr] StartX=12.5 StartY=-32.5 StartZ=0 EndX=12.5 EndY=-34.5 EndZ=0
  constraints (87):
    c: Coincident(g0,g1)
    c: Coincident(g1,g2)
    c: Coincident(g2,g3)
    c: Coincident(g3,g0)
    c: Horizontal(g2)
    c: Vertical(g1)
    c: Vertical(g3)
    c: Coincident(g0,g-1)
    c: Coincident(g4,g5)
    c: Coincident(g5,g6)
    c: Coincident(g6,g7)
    c: Coincident(g7,g4)
    c: Horizontal(g6)
    c: Vertical(g5)
    c: Vertical(g7)
    c: PointOnObject(g4,g-1)
    c: Coincident(g8,g9)
    c: Coincident(g9,g10)
    c: Coincident(g10,g11)
    c: Coincident(g11,g8)
    c: Horizontal(g8)
    c: Horizontal(g10)
    c: Vertical(g9)
    c: Vertical(g11)
    c: PointOnObject(g8,g-1)
    c: Coincident(g12,g13)
    c: Coincident(g13,g14)
    c: Coincident(g14,g15)
    c: Coincident(g15,g12)
    c: Horizontal(g12)
    c: Horizontal(g14)
    c: Vertical(g13)
    c: Vertical(g15)
    c: Coincident(g5,g-3)
    c: Coincident(g2,g-3)
    c: PointOnObject(g16,g-3)
    c: Symmetric(g2,g5,g16)
    c: PointOnObject(g16,g-1)
    c: DistanceX(g8,g8) = 6
    c: DistanceY(g12,g9) = 2
    c: DistanceY(g13,g13) = 8
    c: Horizontal(g0)
    c: DistanceX(g8,g4) = 2.5
    c: Horizontal(g4)
    c: Coincident(g17,g-4)
    c: Coincident(g19,g-6)
    c: Coincident(g20,g-5)
    c: Radius(g20) = 1.5
    c: Equal(g20,g17)
    c: Equal(g20,g18)
    c: Equal(g20,g19)
    c: Coincident(g18,g-7)
    c: DistanceX(g12,g12) = 6
    c: DistanceX(g8,g16) = 1.5
    c: Vertical(g21)
    c: Coincident(g21,g10)
    c: Coincident(g12,g21)
    c: Coincident(g22,g23)
    c: Coincident(g23,g24)
    c: Coincident(g24,g25)
    c: Coincident(g25,g22)
    c: Horizontal(g22)
    c: Horizontal(g24)
    c: Vertical(g23)
    c: Vertical(g25)
    c: Coincident(g26,g27)
    c: Coincident(g27,g28)
    c: Coincident(g28,g29)
    c: Coincident(g29,g26)
    c: Horizontal(g26)
    c: Horizontal(g28)
    c: Vertical(g27)
    c: Vertical(g29)
    c: PointOnObject(g26,g-3)
    c: Equal(g22,g14)
    c: Equal(g14,g28)
    c: Coincident(g30,g14)
    c: Coincident(g30,g22)
    c: Coincident(g31,g24)
    c: Coincident(g31,g28)
    c: Vertical(g31)
    c: Vertical(g30)
    c: Equal(g23,g13)
    c: DistanceY(g31,g31) = 2
    c: DistanceY(g30,g30) = 4
    c: Equal(g9,g27)
    c: Equal(g0,g4)
FEATURE [PartDesign::Pad] Pad004
  BaseFeature = -> Pad003
  Length = 8
  Length2 = 100
  Placement = pos=(0,0,0) rot=(1,0,0;1.5708rad)
  Profile = -> Sketch009
  Type = 0
FEATURE [PartDesign::Fillet] Fillet002
  Base = -> Pad004 [Edge89,Edge91,Edge95,Edge80,Edge101,Edge103,Edge97,Edge85]
  BaseFeature = -> Pad004
  Placement = pos=(0,0,0) rot=(1,0,0;1.5708rad)
  Radius = 2.9
FEATURE [Sketcher::SketchObject] Sketch011
  ExternalGeometry = -> [Fillet002]
  MapMode = 5
  Placement = pos=(0,8,8.278e-13) rot=(-1,0,0;1.5708rad)
  Support = -> [Fillet002]
  sketch-geometry (8):
    g0: LineSegment StartX=0 StartY=0 StartZ=0 EndX=7 EndY=0 EndZ=0
    g1: LineSegment StartX=7 StartY=0 StartZ=0 EndX=7 EndY=-8 EndZ=0
    g2: LineSegment StartX=7 StartY=-8 StartZ=0 EndX=0 EndY=-8 EndZ=0
    g3: LineSegment StartX=0 StartY=-8 StartZ=0 EndX=0 EndY=0 EndZ=0
    g4: LineSegment StartX=28 StartY=0 StartZ=0 EndX=21 EndY=0 EndZ=0
    g5: LineSegment StartX=21 StartY=0 StartZ=0 EndX=21 EndY=-8 EndZ=0
    g6: LineSegment StartX=21 StartY=-8 StartZ=0 EndX=28 EndY=-8 EndZ=0
    g7: LineSegment StartX=28 StartY=-8 StartZ=0 EndX=28 EndY=0 EndZ=0
  constraints (23):
    c: Coincident(g0,g1)
    c: Coincident(g1,g2)
    c: Coincident(g2,g3)
    c: Coincident(g3,g0)
    c: Horizontal(g0)
    c: Horizontal(g2)
    c: Vertical(g1)
    c: Vertical(g3)
    c: Coincident(g0,g-1)
    c: Coincident(g4,g5)
    c: Coincident(g5,g6)
    c: Coincident(g6,g7)
    c: Coincident(g7,g4)
    c: Horizontal(g4)
    c: Horizontal(g6)
    c: Vertical(g5)
    c: Vertical(g7)
    c: PointOnObject(g4,g-1)
    c: PointOnObject(g6,g-3)
    c: DistanceX(g0,g0) = 7
    c: Equal(g4,g0)
    c: Equal(g7,g3)
    c: DistanceY(g7,g7) = 8
FEATURE [PartDesign::Pad] Pad005
  BaseFeature = -> Fillet002
  Length = 8
  Length2 = 100
  Placement = pos=(0,0,0) rot=(1,0,0;1.5708rad)
  Profile = -> Sketch011
  Type = 0
FEATURE [PartDesign::Fillet] Fillet003
  Base = -> Pad005 [Edge139,Edge138,Edge149,Edge144]
  BaseFeature = -> Pad005
  Placement = pos=(0,0,0) rot=(1,0,0;1.5708rad)
  Radius = 3.99
FEATURE [Sketcher::SketchObject] Sketch012
  ExternalGeometry = -> [Fillet003]
  MapMode = 5
  Placement = pos=(0,0,0) rot=(0.707107,0,-0.707107;3.14159rad)
  Support = -> [Fillet003]
  sketch-geometry (1):
    g0: Circle CenterX=-3.99 CenterY=-12.01 CenterZ=0 NormalX=0 NormalY=0 NormalZ=1 AngleXU=0 Radius=3.99
  constraints (2):
    c: Coincident(g0,g-3)
    c: PointOnObject(g-3,g0)
FEATURE [PartDesign::Pad] Pad006
  BaseFeature = -> Fillet003
  Length = 11
  Length2 = 100
  Placement = pos=(0,0,0) rot=(1,0,0;1.5708rad)
  Profile = -> Sketch012
  Type = 0
FEATURE [Sketcher::SketchObject] Sketch013
  ExternalGeometry = -> [Pad006]
  MapMode = 5
  Placement = pos=(28,0,0) rot=(0.707107,0,0.707107;3.14159rad)
  Support = -> [Pad006]
  sketch-geometry (1):
    g0: Circle CenterX=3.99 CenterY=-12.01 CenterZ=0 NormalX=0 NormalY=0 NormalZ=1 AngleXU=0 Radius=3.99
  constraints (2):
    c: Coincident(g0,g-3)
    c: PointOnObject(g-3,g0)
FEATURE [PartDesign::Pad] Pad007
  BaseFeature = -> Pad006
  Length = 11
  Length2 = 100
  Placement = pos=(0,0,0) rot=(1,0,0;1.5708rad)
  Profile = -> Sketch013
  Type = 0
FEATURE [Sketcher::SketchObject] Sketch014
  ExternalGeometry = -> [Pad007]
  MapMode = 5
  Placement = pos=(39,0,0) rot=(0.707107,0,0.707107;3.14159rad)
  Support = -> [Pad007]
  sketch-geometry (1):
    g0: Circle CenterX=3.99 CenterY=-12.01 CenterZ=0 NormalX=0 NormalY=0 NormalZ=1 AngleXU=0 Radius=1.5
  constraints (2):
    c: Coincident(g0,g-3)
    c: Radius(g0) = 1.5
FEATURE [PartDesign::Pocket] Pocket001
  BaseFeature = -> Pad007
  Length = 52
  Length2 = 100
  Placement = pos=(0,0,0) rot=(1,0,0;1.5708rad)
  Profile = -> Sketch014
  Type = 0
FEATURE [PartDesign::Chamfer] Chamfer001
  Base = -> Pocket001 [Edge30,Edge175]
  BaseFeature = -> Pocket001
  Placement = pos=(0,0,0) rot=(1,0,0;1.5708rad)
  Size = 1.2
FEATURE [Sketcher::SketchObject] Sketch015
  MapMode = 5
  Placement = pos=(0,0,0) rot=(0.707107,0,-0.707107;3.14159rad)
  Support = -> [Chamfer001]
  sketch-geometry (4):
    g0: LineSegment StartX=-5.5 StartY=1 StartZ=0 EndX=-2.5 EndY=1 EndZ=0
    g1: LineSegment StartX=-2.5 StartY=1 StartZ=0 EndX=-2.5 EndY=-9 EndZ=0
    g2: LineSegment StartX=-2.5 StartY=-9 StartZ=0 EndX=-5.5 EndY=-9 EndZ=0
    g3: LineSegment StartX=-5.5 StartY=-9 StartZ=0 EndX=-5.5 EndY=1 EndZ=0
  constraints (12):
    c: Coincident(g0,g1)
    c: Coincident(g1,g2)
    c: Coincident(g2,g3)
    c: Coincident(g3,g0)
    c: Horizontal(g0)
    c: Horizontal(g2)
    c: Vertical(g1)
    c: Vertical(g3)
    c: DistanceY(g1,g1) = 10
    c: DistanceY(g-1,g0) = 1
    c: DistanceX(g0,g-1) = 2.5
    c: DistanceX(g0,g0) = 3
FEATURE [PartDesign::Pad] Pad008
  BaseFeature = -> Chamfer001
  Length = 9
  Length2 = 100
  Placement = pos=(0,0,0) rot=(1,0,0;1.5708rad)
  Profile = -> Sketch015
  Type = 0
FEATURE [Sketcher::SketchObject] Sketch016
  MapMode = 5
  Placement = pos=(28,0,0) rot=(0.707107,0,0.707107;3.14159rad)
  Support = -> [Pad008]
  sketch-geometry (4):
    g0: LineSegment StartX=2.5 StartY=1 StartZ=0 EndX=5.5 EndY=1 EndZ=0
    g1: LineSegment StartX=5.5 StartY=1 StartZ=0 EndX=5.5 EndY=-9 EndZ=0
    g2: LineSegment StartX=5.5 StartY=-9 StartZ=0 EndX=2.5 EndY=-9 EndZ=0
    g3: LineSegment StartX=2.5 StartY=-9 StartZ=0 EndX=2.5 EndY=1 EndZ=0
  constraints (12):
    c: Coincident(g0,g1)
    c: Coincident(g1,g2)
    c: Coincident(g2,g3)
    c: Coincident(g3,g0)
    c: Horizontal(g0)
    c: Horizontal(g2)
    c: Vertical(g1)
    c: Vertical(g3)
    c: DistanceY(g1,g1) = 10
    c: DistanceX(g0,g0) = 3
    c: DistanceX(g-1,g0) = 2.5
    c: DistanceY(g-1,g0) = 1
FEATURE [PartDesign::Pad] Pad009
  BaseFeature = -> Pad008
  Length = 9
  Length2 = 100
  Placement = pos=(0,0,0) rot=(1,0,0;1.5708rad)
  Profile = -> Sketch016
  Type = 0
FEATURE [PartDesign::Chamfer] Chamfer002
  Base = -> Pad009 [Edge178,Edge20]
  BaseFeature = -> Pad009
  Placement = pos=(0,0,0) rot=(1,0,0;1.5708rad)
  Size = 8.9999
FEATURE [PartDesign::Chamfer] Chamfer003
  Base = -> Chamfer002 [Edge13,Edge207]
  BaseFeature = -> Chamfer002
  Placement = pos=(0,0,0) rot=(1,0,0;1.5708rad)
  Size = 0.7
FEATURE [Sketcher::SketchObject] Sketch017
  ExternalGeometry = -> [Chamfer003]
  MapMode = 5
  Placement = pos=(21,0,0) rot=(0.707107,0,-0.707107;3.14159rad)
  Support = -> [Chamfer003]
  sketch-geometry (7):
    g0: LineSegment StartX=-2.49 StartY=-14.6081 StartZ=0 EndX=-0.99 EndY=-12.01 EndZ=0
    g1: LineSegment StartX=-0.99 StartY=-12.01 StartZ=0 EndX=-2.49 EndY=-9.41192 EndZ=0
    g2: LineSegment StartX=-2.49 StartY=-9.41192 StartZ=0 EndX=-5.49 EndY=-9.41192 EndZ=0
    g3: LineSegment StartX=-5.49 StartY=-9.41192 StartZ=0 EndX=-6.99 EndY=-12.01 EndZ=0
    g4: LineSegment StartX=-6.99 StartY=-12.01 StartZ=0 EndX=-5.49 EndY=-14.6081 EndZ=0
    g5: LineSegment StartX=-5.49 StartY=-14.6081 StartZ=0 EndX=-2.49 EndY=-14.6081 EndZ=0
    g6: Circle [constr] CenterX=-3.99 CenterY=-12.01 CenterZ=0 NormalX=0 NormalY=0 NormalZ=1 AngleXU=0 Radius=3
  constraints (16):
    c: Coincident(g0,g1)
    c: Coincident(g1,g2)
    c: Coincident(g2,g3)
    c: Coincident(g3,g4)
    c: Coincident(g4,g5)
    c: Coincident(g5,g0)
    c: Equal(g0, g1-g5) x5
    c: PointOnObject(g0,g6)
    c: PointOnObject(g1,g6)
    c: PointOnObject(g2,g6)
    c: PointOnObject(g3,g6)
    c: PointOnObject(g4,g6)
    c: PointOnObject(g5,g6)
    c: Coincident(g-3,g6)
    c: Radius(g6) = 3
    c: Horizontal(g2)
FEATURE [PartDesign::Pocket] Pocket002
  BaseFeature = -> Chamfer003
  Length = 3
  Length2 = 100
  Placement = pos=(0,0,0) rot=(1,0,0;1.5708rad)
  Profile = -> Sketch017
  Type = 0
FEATURE [Sketcher::SketchObject] Sketch018
  ExternalGeometry = -> [Pocket002]
  MapMode = 5
  Placement = pos=(7,0,0) rot=(0.707107,0,0.707107;3.14159rad)
  Support = -> [Pocket002]
  sketch-geometry (7):
    g0: LineSegment StartX=5.49 StartY=-14.6081 StartZ=0 EndX=6.99 EndY=-12.01 EndZ=0
    g1: LineSegment StartX=6.99 StartY=-12.01 StartZ=0 EndX=5.49 EndY=-9.41192 EndZ=0
    g2: LineSegment StartX=5.49 StartY=-9.41192 StartZ=0 EndX=2.49 EndY=-9.41192 EndZ=0
    g3: LineSegment StartX=2.49 StartY=-9.41192 StartZ=0 EndX=0.99 EndY=-12.01 EndZ=0
    g4: LineSegment StartX=0.99 StartY=-12.01 StartZ=0 EndX=2.49 EndY=-14.6081 EndZ=0
    g5: LineSegment StartX=2.49 StartY=-14.6081 StartZ=0 EndX=5.49 EndY=-14.6081 EndZ=0
    g6: Circle [constr] CenterX=3.99 CenterY=-12.01 CenterZ=0 NormalX=0 NormalY=0 NormalZ=1 AngleXU=0 Radius=3
  constraints (16):
    c: Coincident(g0,g1)
    c: Coincident(g1,g2)
    c: Coincident(g2,g3)
    c: Coincident(g3,g4)
    c: Coincident(g4,g5)
    c: Coincident(g5,g0)
    c: Equal(g0, g1-g5) x5
    c: PointOnObject(g0,g6)
    c: PointOnObject(g1,g6)
    c: PointOnObject(g2,g6)
    c: PointOnObject(g3,g6)
    c: PointOnObject(g4,g6)
    c: PointOnObject(g5,g6)
    c: Coincident(g6,g-3)
    c: Horizontal(g5)
    c: Radius(g6) = 3
FEATURE [PartDesign::Pocket] Pocket003
  BaseFeature = -> Pocket002
  Length = 3
  Length2 = 100
  Placement = pos=(0,0,0) rot=(1,0,0;1.5708rad)
  Profile = -> Sketch018
  Type = 0
FEATURE [Sketcher::SketchObject] Sketch019
  ExternalGeometry = -> [Pocket003]
  MapMode = 5
  Placement = pos=(0,0,0) rot=(1,0,0;3.14159rad)
  Support = -> [Pocket003]
  sketch-geometry (2):
    g0: Circle CenterX=15.5 CenterY=3 CenterZ=0 NormalX=0 NormalY=0 NormalZ=1 AngleXU=0 Radius=1.5
    g1: LineSegment [constr] StartX=15.5 StartY=-8 StartZ=0 EndX=15.5 EndY=6 EndZ=0
  constraints (7):
    c: PointOnObject(g1,g-4)
    c: PointOnObject(g1,g-3)
    c: PointOnObject(g0,g1)
    c: Vertical(g1)
    c: Symmetric(g-4,g-4,g1)
    c: Radius(g0) = 1.5
    c: DistanceY(g0,g-3) = 3
FEATURE [PartDesign::Pocket] Pocket004
  BaseFeature = -> Pocket003
  Length = 15
  Length2 = 100
  Placement = pos=(0,0,0) rot=(1,0,0;1.5708rad)
  Profile = -> Sketch019
  Type = 0
FEATURE [Sketcher::SketchObject] Sketch020
  ExternalGeometry = -> [Pocket004]
  MapMode = 5
  Placement = pos=(0,8,8.278e-13) rot=(-1,0,0;1.5708rad)
  Support = -> [Pocket004]
  sketch-geometry (4):
    g0: Circle CenterX=4 CenterY=-12.5 CenterZ=0 NormalX=0 NormalY=0 NormalZ=1 AngleXU=0 Radius=3.2
    g1: Circle CenterX=4 CenterY=-32.5 CenterZ=0 NormalX=0 NormalY=0 NormalZ=1 AngleXU=0 Radius=3.2
    g2: Circle CenterX=24 CenterY=-32.5 CenterZ=0 NormalX=0 NormalY=0 NormalZ=1 AngleXU=0 Radius=3.2
    g3: Circle CenterX=24 CenterY=-12.5 CenterZ=0 NormalX=0 NormalY=0 NormalZ=1 AngleXU=0 Radius=3.2
  constraints (8):
    c: Coincident(g0,g-3)
    c: Coincident(g1,g-4)
    c: Coincident(g2,g-5)
    c: Coincident(g3,g-6)
    c: Radius(g3) = 3.2
    c: Equal(g3,g0)
    c: Equal(g3,g1)
    c: Equal(g3,g2)
FEATURE [PartDesign::Pocket] Pocket005
  BaseFeature = -> Pocket004
  Length = 3
  Length2 = 100
  Placement = pos=(0,0,0) rot=(1,0,0;1.5708rad)
  Profile = -> Sketch020
  Type = 0
FEATURE [PartDesign::Chamfer] Chamfer004
  Base = -> Pocket005 [Edge91,Edge89,Edge173,Edge87,Edge177,Edge85,Edge179,Edge175]
  BaseFeature = -> Pocket005
  Placement = pos=(0,0,0) rot=(1,0,0;1.5708rad)
  Size = 2
FEATURE [PartDesign::Body] Body006  label="carriage_belt_holder"
  Group = -> [Sketch008,Pad003,Sketch009,Pad004,Fillet002,Sketch011,Pad005,Fillet003,Sketch012,Pad006,Sketch013,Pad007,Sketch014,Pocket001,Chamfer001,Sketch015,Pad008,Sketch016,Pad009,Chamfer002,Chamfer003,Sketch017,Pocket002,Sketch018,Pocket003,Sketch019,Pocket004,Sketch020,Pocket005,Chamfer004]
  Origin = -> Origin006
  Placement = pos=(-14,27.5,3) rot=(0,0,1;0rad)
  Tip = -> Chamfer004
FEATURE [Sketcher::SketchObject] Sketch021
  MapMode = 5
  Placement = pos=(0,0,0) rot=(1,0,0;1.5708rad)
  Support = -> [XZ_Plane007]
  sketch-geometry (20):
    g0: LineSegment StartX=0 StartY=0 StartZ=0 EndX=28 EndY=0 EndZ=0
    g1: LineSegment StartX=28 StartY=0 StartZ=0 EndX=28 EndY=45 EndZ=0
    g2: LineSegment StartX=28 StartY=45 StartZ=0 EndX=0 EndY=45 EndZ=0
    g3: LineSegment StartX=0 StartY=45 StartZ=0 EndX=0 EndY=0 EndZ=0
    g4: LineSegment [constr] StartX=4 StartY=32.5 StartZ=0 EndX=24 EndY=32.5 EndZ=0
    g5: LineSegment [constr] StartX=24 StartY=32.5 StartZ=0 EndX=24 EndY=12.5 EndZ=0
    g6: LineSegment [constr] StartX=24 StartY=12.5 StartZ=0 EndX=4 EndY=12.5 EndZ=0
    g7: LineSegment [constr] StartX=4 StartY=12.5 StartZ=0 EndX=4 EndY=32.5 EndZ=0
    g8: LineSegment [constr] StartX=0 StartY=22.5 StartZ=0 EndX=4 EndY=22.5 EndZ=0
    g9: LineSegment [constr] StartX=14 StartY=45 StartZ=0 EndX=14 EndY=32.5 EndZ=0
    g10: Circle CenterX=4 CenterY=32.5 CenterZ=0 NormalX=0 NormalY=0 NormalZ=1 AngleXU=0 Radius=1.5
    g11: Circle CenterX=24 CenterY=32.5 CenterZ=0 NormalX=0 NormalY=0 NormalZ=1 AngleXU=0 Radius=1.5
    g12: Circle CenterX=4 CenterY=12.5 CenterZ=0 NormalX=0 NormalY=0 NormalZ=1 AngleXU=0 Radius=1.5
    g13: Circle CenterX=24 CenterY=12.5 CenterZ=0 NormalX=0 NormalY=0 NormalZ=1 AngleXU=0 Radius=1.5
    g14: LineSegment [constr] StartX=0 StartY=45 StartZ=0 EndX=-12 EndY=25.5 EndZ=0
    g15: LineSegment [constr] StartX=-12 StartY=25.5 StartZ=0 EndX=-12 EndY=19.5 EndZ=0
    g16: LineSegment [constr] StartX=-12 StartY=19.5 StartZ=0 EndX=0 EndY=0 EndZ=0
    g17: LineSegment [constr] StartX=28 StartY=0 StartZ=0 EndX=40 EndY=19.5 EndZ=0
    g18: LineSegment [constr] StartX=40 StartY=19.5 StartZ=0 EndX=40 EndY=25.5 EndZ=0
    g19: LineSegment [constr] StartX=40 StartY=25.5 StartZ=0 EndX=28 EndY=45 EndZ=0
  constraints (54):
    c: Coincident(g0,g1)
    c: Coincident(g1,g2)
    c: Coincident(g2,g3)
    c: Coincident(g3,g0)
    c: Horizontal(g0)
    c: Horizontal(g2)
    c: Vertical(g1)
    c: Vertical(g3)
    c: PointOnObject(g0,g-1)
    c: Coincident(g0,g-1)
    c: DistanceX(g0,g0) = 28
    c: DistanceY(g1,g1) = 45
    c: Coincident(g4,g5)
    c: Coincident(g5,g6)
    c: Coincident(g6,g7)
    c: Coincident(g7,g4)
    c: Horizontal(g6)
    c: Vertical(g5)
    c: Vertical(g7)
    c: PointOnObject(g8,g3)
    c: PointOnObject(g8,g7)
    c: Symmetric(g6,g4,g8)
    c: Symmetric(g-1,g2,g8)
    c: PointOnObject(g9,g2)
    c: PointOnObject(g9,g4)
    c: Vertical(g9)
    c: Symmetric(g4,g4,g9)
    c: Symmetric(g1,g2,g9)
    c: DistanceX(g4,g4) = 20
    c: DistanceY(g5,g5) = 20
    c: Coincident(g10,g4)
    c: Coincident(g11,g4)
    c: Coincident(g12,g6)
    c: Coincident(g13,g5)
    c: Radius(g13) = 1.5
    c: Equal(g13,g11)
    c: Equal(g13,g10)
    c: Equal(g13,g12)
    c: Coincident(g14,g2)
    c: Coincident(g15,g14)
    c: Vertical(g15)
    c: Coincident(g16,g15)
    c: Coincident(g16,g-1)
    c: Coincident(g17,g0)
    c: Coincident(g18,g17)
    c: Vertical(g18)
    c: Coincident(g19,g18)
    c: Coincident(g19,g1)
    c: Equal(g18,g15)
    c: Equal(g19,g14)
    c: Equal(g16,g17)
    c: DistanceY(g15,g15) = 6
    c: Equal(g16,g14)
    c: DistanceX(g14,g18) = 52
FEATURE [PartDesign::Pad] Pad010
  Length = 6
  Length2 = 100
  Placement = pos=(0,0,0) rot=(1,0,0;1.5708rad)
  Profile = -> Sketch021
  Type = 0
FEATURE [Sketcher::SketchObject] Sketch022
  ExternalGeometry = -> [Pad010]
  MapMode = 5
  Placement = pos=(0,-1e-16,0) rot=(-1,0,0;1.5708rad)
  Support = -> [Pad010]
  sketch-geometry (22):
    g0: LineSegment StartX=0 StartY=0 StartZ=0 EndX=7 EndY=0 EndZ=0
    g1: LineSegment StartX=7 StartY=0 StartZ=0 EndX=7 EndY=-45 EndZ=0
    g2: LineSegment StartX=7 StartY=-45 StartZ=0 EndX=0 EndY=-45 EndZ=0
    g3: LineSegment StartX=0 StartY=-45 StartZ=0 EndX=0 EndY=0 EndZ=0
    g4: LineSegment StartX=21 StartY=0 StartZ=0 EndX=28 EndY=0 EndZ=0
    g5: LineSegment StartX=28 StartY=0 StartZ=0 EndX=28 EndY=-45 EndZ=0
    g6: LineSegment StartX=28 StartY=-45 StartZ=0 EndX=21 EndY=-45 EndZ=0
    g7: LineSegment StartX=21 StartY=-45 StartZ=0 EndX=21 EndY=0 EndZ=0
    g8: LineSegment StartX=12.5 StartY=0 StartZ=0 EndX=18.5 EndY=0 EndZ=0
    g9: LineSegment StartX=18.5 StartY=0 StartZ=0 EndX=18.5 EndY=-10 EndZ=0
    g10: LineSegment StartX=18.5 StartY=-10 StartZ=0 EndX=12.5 EndY=-10 EndZ=0
    g11: LineSegment StartX=12.5 StartY=-10 StartZ=0 EndX=12.5 EndY=0 EndZ=0
    g12: LineSegment StartX=12.5 StartY=-12 StartZ=0 EndX=18.5 EndY=-12 EndZ=0
    g13: LineSegment StartX=18.5 StartY=-12 StartZ=0 EndX=18.5 EndY=-18 EndZ=0
    g14: LineSegment StartX=18.5 StartY=-18 StartZ=0 EndX=12.5 EndY=-18 EndZ=0
    g15: LineSegment StartX=12.5 StartY=-18 StartZ=0 EndX=12.5 EndY=-12 EndZ=0
    g16: Circle CenterX=24 CenterY=-12.5 CenterZ=0 NormalX=0 NormalY=0 NormalZ=1 AngleXU=0 Radius=1.5
    g17: Circle CenterX=4 CenterY=-12.5 CenterZ=0 NormalX=0 NormalY=0 NormalZ=1 AngleXU=0 Radius=1.5
    g18: Circle CenterX=4 CenterY=-32.5 CenterZ=0 NormalX=0 NormalY=0 NormalZ=1 AngleXU=0 Radius=1.5
    g19: Circle CenterX=24 CenterY=-32.5 CenterZ=0 NormalX=0 NormalY=0 NormalZ=1 AngleXU=0 Radius=1.5
    g20: LineSegment [constr] StartX=12.5 StartY=-12 StartZ=0 EndX=12.5 EndY=-10 EndZ=0
    g21: LineSegment StartX=12.5 StartY=-45 StartZ=0 EndX=18.5 EndY=-45 EndZ=0
  constraints (57):
    c: Coincident(g0,g1)
    c: Coincident(g1,g2)
    c: Coincident(g2,g3)
    c: Coincident(g3,g0)
    c: Horizontal(g2)
    c: Vertical(g1)
    c: Vertical(g3)
    c: Coincident(g0,g-1)
    c: Coincident(g4,g5)
    c: Coincident(g5,g6)
    c: Coincident(g6,g7)
    c: Coincident(g7,g4)
    c: Horizontal(g6)
    c: Vertical(g5)
    c: Vertical(g7)
    c: PointOnObject(g4,g-1)
    c: Coincident(g8,g9)
    c: Coincident(g9,g10)
    c: Coincident(g10,g11)
    c: Coincident(g11,g8)
    c: Horizontal(g8)
    c: Horizontal(g10)
    c: Vertical(g9)
    c: Vertical(g11)
    c: PointOnObject(g8,g-1)
    c: Coincident(g12,g13)
    c: Coincident(g13,g14)
    c: Coincident(g14,g15)
    c: Coincident(g15,g12)
    c: Horizontal(g12)
    c: Horizontal(g14)
    c: Vertical(g13)
    c: Vertical(g15)
    c: Coincident(g5,g-3)
    c: Coincident(g2,g-3)
    c: DistanceX(g8,g8) = 6
    c: DistanceY(g12,g9) = 2
    c: DistanceY(g13,g13) = 6
    c: Horizontal(g0)
    c: DistanceX(g8,g4) = 2.5
    c: Horizontal(g4)
    c: Coincident(g16,g-4)
    c: Coincident(g18,g-6)
    c: Coincident(g19,g-5)
    c: Radius(g19) = 1.5
    c: Equal(g19,g16)
    c: Equal(g19,g17)
    c: Equal(g19,g18)
    c: Coincident(g17,g-7)
    c: DistanceX(g12,g12) = 6
    c: Vertical(g20)
    c: Coincident(g20,g10)
    c: Coincident(g12,g20)
    c: Horizontal(g21)
    c: PointOnObject(g21,g-3)
    c: Equal(g0,g4)
    c: DistanceY(g9,g9) = 10
FEATURE [PartDesign::Pad] Pad011
  BaseFeature = -> Pad010
  Length = 8
  Length2 = 100
  Placement = pos=(0,0,0) rot=(1,0,0;1.5708rad)
  Profile = -> Sketch022
  Type = 0
FEATURE [Sketcher::SketchObject] Sketch032
  MapMode = 5
  Placement = pos=(0,8,8.14e-13) rot=(-1,0,0;1.5708rad)
  sketch-geometry (4):
    g0: Circle CenterX=4 CenterY=-12.5 CenterZ=0 NormalX=0 NormalY=0 NormalZ=1 AngleXU=0 Radius=3.5
    g1: Circle CenterX=4 CenterY=-32.5 CenterZ=0 NormalX=0 NormalY=0 NormalZ=1 AngleXU=0 Radius=3.5
    g2: Circle CenterX=24 CenterY=-32.5 CenterZ=0 NormalX=0 NormalY=0 NormalZ=1 AngleXU=0 Radius=3.5
    g3: Circle CenterX=24 CenterY=-12.5 CenterZ=0 NormalX=0 NormalY=0 NormalZ=1 AngleXU=0 Radius=3.5
  constraints (4):
    c: Radius(g1) = 3.5
    c: Equal(g1,g0)
    c: Equal(g1,g3)
    c: Equal(g1,g2)
FEATURE [PartDesign::Pocket] Pocket010
  BaseFeature = -> Pad011
  Length = 3
  Length2 = 100
  Placement = pos=(0,0,0) rot=(1,0,0;1.5708rad)
  Profile = -> Sketch032
  Type = 0
FEATURE [Sketcher::SketchObject] Sketch033
  ExternalGeometry = -> [Pocket010]
  MapMode = 5
  Placement = pos=(0,-4.635e-12,45) rot=(0,0,1;3.14159rad)
  Support = -> [Pocket010]
  sketch-geometry (5):
    g0: LineSegment StartX=-22 StartY=6 StartZ=0 EndX=-8 EndY=6 EndZ=0
    g1: LineSegment StartX=-21 StartY=0 StartZ=0 EndX=-10 EndY=0 EndZ=0
    g2: LineSegment StartX=-21 StartY=0 StartZ=0 EndX=-22 EndY=6 EndZ=0
    g3: LineSegment StartX=-10 StartY=0 StartZ=0 EndX=-8 EndY=6 EndZ=0
    g4: LineSegment [constr] StartX=-15 StartY=0 StartZ=0 EndX=-15 EndY=6 EndZ=0
  constraints (15):
    c: PointOnObject(g1,g-3)
    c: PointOnObject(g1,g-3)
    c: Horizontal(g0)
    c: PointOnObject(g0,g-4)
    c: Coincident(g2,g1)
    c: Coincident(g2,g0)
    c: Coincident(g3,g1)
    c: Coincident(g3,g0)
    c: PointOnObject(g4,g1)
    c: PointOnObject(g4,g0)
    c: DistanceX(g0,g0) = 14
    c: Symmetric(g0,g0,g4)
    c: DistanceX(g1,g1) = 11
    c: Coincident(g1,g-3)
    c: DistanceX(g0,g1) = 1
FEATURE [PartDesign::Pocket] Pocket011
  BaseFeature = -> Pocket010
  Length = 27
  Length2 = 100
  Placement = pos=(0,0,0) rot=(1,0,0;1.5708rad)
  Profile = -> Sketch033
  Type = 0
FEATURE [Sketcher::SketchObject] Sketch034
  ExternalGeometry = -> [Pocket011]
  MapMode = 5
  Placement = pos=(0,-1.8545e-12,18) rot=(0,0,1;3.14159rad)
  Support = -> [Pocket011]
  sketch-geometry (2):
    g0: Circle CenterX=-15.5 CenterY=3 CenterZ=0 NormalX=0 NormalY=0 NormalZ=1 AngleXU=0 Radius=1.5
    g1: LineSegment [constr] StartX=-15.5 StartY=-8 StartZ=0 EndX=-15.5 EndY=3 EndZ=0
  constraints (6):
    c: Coincident(g1,g0)
    c: Vertical(g1)
    c: Radius(g0) = 1.5
    c: DistanceY(g1,g1) = 11
    c: PointOnObject(g1,g-3)
    c: Symmetric(g-3,g-3,g1)
FEATURE [PartDesign::Pocket] Pocket012
  BaseFeature = -> Pocket011
  Length = 19
  Length2 = 100
  Placement = pos=(0,0,0) rot=(1,0,0;1.5708rad)
  Profile = -> Sketch034
  Type = 0
FEATURE [Sketcher::SketchObject] Sketch035
  ExternalGeometry = -> [Pocket012]
  MapMode = 5
  Placement = pos=(0,0,0) rot=(0.707107,0,-0.707107;3.14159rad)
  Support = -> [Pocket012]
  sketch-geometry (1):
    g0: Circle CenterX=-5 CenterY=-3 CenterZ=0 NormalX=0 NormalY=0 NormalZ=1 AngleXU=0 Radius=5
  constraints (3):
    c: Radius(g0) = 5
    c: DistanceX(g0,g-3) = 5
    c: DistanceY(g-3,g0) = 5
FEATURE [Sketcher::SketchObject] Sketch036
  ExternalGeometry = -> [Pocket012]
  MapMode = 5
  Placement = pos=(28,0,0) rot=(0.707107,0,0.707107;3.14159rad)
  Support = -> [Pocket012]
  sketch-geometry (1):
    g0: Circle CenterX=5 CenterY=-3 CenterZ=0 NormalX=0 NormalY=0 NormalZ=1 AngleXU=0 Radius=5
  constraints (3):
    c: DistanceX(g-3,g0) = 5
    c: DistanceY(g-3,g0) = 5
    c: Radius(g0) = 5
FEATURE [PartDesign::Pad] Pad012
  BaseFeature = -> Pocket012
  Length = 11
  Length2 = 100
  Placement = pos=(0,0,0) rot=(1,0,0;1.5708rad)
  Profile = -> Sketch035
  Type = 0
FEATURE [PartDesign::Pad] Pad013
  BaseFeature = -> Pad012
  Length = 11
  Length2 = 100
  Placement = pos=(0,0,0) rot=(1,0,0;1.5708rad)
  Profile = -> Sketch036
  Type = 0
FEATURE [Sketcher::SketchObject] Sketch037
  ExternalGeometry = -> [Pad013]
  MapMode = 5
  Placement = pos=(-11,0,-2.4e-15) rot=(0.707107,0,-0.707107;3.14159rad)
  Support = -> [Pad013]
  sketch-geometry (1):
    g0: Circle CenterX=-5 CenterY=-3 CenterZ=0 NormalX=0 NormalY=0 NormalZ=1 AngleXU=0 Radius=1.5
  constraints (2):
    c: Coincident(g0,g-3)
    c: Radius(g0) = 1.5
FEATURE [PartDesign::Pocket] Pocket013
  BaseFeature = -> Pad013
  Length = 20
  Length2 = 100
  Placement = pos=(0,0,0) rot=(1,0,0;1.5708rad)
  Profile = -> Sketch037
  Type = 0
FEATURE [Sketcher::SketchObject] Sketch038
  ExternalGeometry = -> [Pocket013]
  MapMode = 5
  Placement = pos=(39,0,-1.83e-14) rot=(0.707107,0,0.707107;3.14159rad)
  Support = -> [Pocket013]
  sketch-geometry (1):
    g0: Circle CenterX=5 CenterY=-3 CenterZ=0 NormalX=0 NormalY=0 NormalZ=1 AngleXU=0 Radius=1.5
  constraints (2):
    c: Coincident(g0,g-3)
    c: Radius(g0) = 1.5
FEATURE [PartDesign::Pocket] Pocket014
  BaseFeature = -> Pocket013
  Length = 20
  Length2 = 100
  Placement = pos=(0,0,0) rot=(1,0,0;1.5708rad)
  Profile = -> Sketch038
  Type = 0
FEATURE [PartDesign::Chamfer] Chamfer005
  Base = -> Pocket014 [Edge92,Edge56]
  BaseFeature = -> Pocket014
  Placement = pos=(0,0,0) rot=(1,0,0;1.5708rad)
  Size = 2
FEATURE [PartDesign::Chamfer] Chamfer006
  Base = -> Chamfer005 [Edge125,Edge2]
  BaseFeature = -> Chamfer005
  Placement = pos=(0,0,0) rot=(1,0,0;1.5708rad)
  Size = 2
FEATURE [PartDesign::Chamfer] Chamfer007
  Base = -> Chamfer006 [Edge127,Edge2]
  BaseFeature = -> Chamfer006
  Placement = pos=(0,0,0) rot=(1,0,0;1.5708rad)
  Size = 2
FEATURE [Sketcher::SketchObject] Sketch039
  MapMode = 5
  Placement = pos=(0,0,0) rot=(0.707107,0,-0.707107;3.14159rad)
  Support = -> [Chamfer007]
  sketch-geometry (4):
    g0: LineSegment StartX=-17 StartY=-2 StartZ=0 EndX=-8 EndY=-2 EndZ=0
    g1: LineSegment StartX=-8 StartY=-2 StartZ=0 EndX=-8 EndY=-4 EndZ=0
    g2: LineSegment StartX=-8 StartY=-4 StartZ=0 EndX=-17 EndY=-4 EndZ=0
    g3: LineSegment StartX=-17 StartY=-4 StartZ=0 EndX=-17 EndY=-2 EndZ=0
  constraints (12):
    c: Coincident(g0,g1)
    c: Coincident(g1,g2)
    c: Coincident(g2,g3)
    c: Coincident(g3,g0)
    c: Horizontal(g0)
    c: Horizontal(g2)
    c: Vertical(g1)
    c: Vertical(g3)
    c: DistanceX(g2,g2) = 9
    c: DistanceY(g3,g3) = 2
    c: DistanceX(g0,g-1) = 8
    c: DistanceY(g0,g-1) = 2
FEATURE [PartDesign::Pad] Pad014
  BaseFeature = -> Chamfer007
  Length = 8
  Length2 = 100
  Placement = pos=(0,0,0) rot=(1,0,0;1.5708rad)
  Profile = -> Sketch039
  Type = 0
FEATURE [Sketcher::SketchObject] Sketch040
  MapMode = 5
  Placement = pos=(28,0,0) rot=(0.707107,0,0.707107;3.14159rad)
  Support = -> [Pad014]
  sketch-geometry (4):
    g0: LineSegment StartX=8 StartY=-2 StartZ=0 EndX=16 EndY=-2 EndZ=0
    g1: LineSegment StartX=16 StartY=-2 StartZ=0 EndX=16 EndY=-4 EndZ=0
    g2: LineSegment StartX=16 StartY=-4 StartZ=0 EndX=8 EndY=-4 EndZ=0
    g3: LineSegment StartX=8 StartY=-4 StartZ=0 EndX=8 EndY=-2 EndZ=0
  constraints (12):
    c: Coincident(g0,g1)
    c: Coincident(g1,g2)
    c: Coincident(g2,g3)
    c: Coincident(g3,g0)
    c: Horizontal(g0)
    c: Horizontal(g2)
    c: Vertical(g1)
    c: Vertical(g3)
    c: DistanceY(g1,g1) = 2
    c: DistanceX(g0,g0) = 8
    c: DistanceY(g0,g-1) = 2
    c: DistanceX(g-1,g0) = 8
FEATURE [PartDesign::Pad] Pad015
  BaseFeature = -> Pad014
  Length = 8
  Length2 = 100
  Placement = pos=(0,0,0) rot=(1,0,0;1.5708rad)
  Profile = -> Sketch040
  Type = 0
FEATURE [PartDesign::Chamfer] Chamfer008
  Base = -> Pad015 [Edge59,Edge185]
  BaseFeature = -> Pad015
  Placement = pos=(0,0,0) rot=(1,0,0;1.5708rad)
  Size = 6
FEATURE [Sketcher::SketchObject] Sketch041
  ExternalGeometry = -> [Chamfer008]
  MapMode = 5
  Placement = pos=(0,-6,-6.208e-13) rot=(1,0,0;1.5708rad)
  Support = -> [Chamfer008]
  sketch-geometry (4):
    g0: LineSegment StartX=12.5 StartY=15 StartZ=0 EndX=18.5 EndY=15 EndZ=0
    g1: LineSegment StartX=18.5 StartY=15 StartZ=0 EndX=18.5 EndY=12.7 EndZ=0
    g2: LineSegment StartX=18.5 StartY=12.7 StartZ=0 EndX=12.5 EndY=12.7 EndZ=0
    g3: LineSegment StartX=12.5 StartY=12.7 StartZ=0 EndX=12.5 EndY=15 EndZ=0
  constraints (12):
    c: Coincident(g0,g1)
    c: Coincident(g1,g2)
    c: Coincident(g2,g3)
    c: Coincident(g3,g0)
    c: Horizontal(g0)
    c: Horizontal(g2)
    c: Vertical(g1)
    c: Vertical(g3)
    c: DistanceX(g0,g0) = 6
    c: DistanceY(g1,g1) = 2.3
    c: DistanceY(g0,g-3) = 3
    c: DistanceX(g0,g-3) = 3.5
FEATURE [PartDesign::Pocket] Pocket015
  BaseFeature = -> Chamfer008
  Length = 6
  Length2 = 100
  Placement = pos=(0,0,0) rot=(1,0,0;1.5708rad)
  Profile = -> Sketch041
  Type = 0
FEATURE [Sketcher::SketchObject] Sketch042
  MapMode = 5
  Support = -> [XY_Plane008]
  sketch-geometry (8):
    g0: LineSegment StartX=-5.9 StartY=0 StartZ=0 EndX=7.9 EndY=0 EndZ=0
    g1: LineSegment StartX=-5.9 StartY=0 StartZ=0 EndX=-3.9 EndY=6 EndZ=0
    g2: LineSegment StartX=-3.9 StartY=6 StartZ=0 EndX=-1.5 EndY=6 EndZ=0
    g3: LineSegment StartX=-1.5 StartY=6 StartZ=0 EndX=-1.5 EndY=14 EndZ=0
    g4: LineSegment StartX=-1.5 StartY=14 StartZ=0 EndX=6.9 EndY=14 EndZ=0
    g5: LineSegment StartX=6.9 StartY=14 StartZ=0 EndX=6.9 EndY=6 EndZ=0
    g6: LineSegment StartX=6.9 StartY=6 StartZ=0 EndX=7.9 EndY=0 EndZ=0
    g7: Circle CenterX=1.5 CenterY=3 CenterZ=0 NormalX=0 NormalY=0 NormalZ=1 AngleXU=0 Radius=1.5
  constraints (24):
    c: PointOnObject(g0,g-1)
    c: PointOnObject(g0,g-1)
    c: Coincident(g1,g0)
    c: Coincident(g2,g1)
    c: Horizontal(g2)
    c: Coincident(g3,g2)
    c: Coincident(g4,g3)
    c: Horizontal(g4)
    c: Coincident(g5,g4)
    c: Vertical(g5)
    c: Coincident(g0,g6)
    c: Coincident(g5,g6)
    c: Vertical(g3)
    c: Equal(g3,g5)
    c: DistanceX(g-1,g0) = 7.9
    c: DistanceX(g0,g-1) = 5.9
    c: DistanceX(g1,g5) = 10.8
    c: DistanceX(g1,g2) = 2.4
    c: DistanceY(g-1,g2) = 6
    c: DistanceY(g3,g3) = 8
    c: DistanceX(g-1,g4) = 6.9
    c: DistanceX(g-1,g7) = 1.5
    c: DistanceY(g-1,g7) = 3
    c: Radius(g7) = 1.5
FEATURE [PartDesign::Pad] Pad016
  Length = 20
  Length2 = 100
  Profile = -> Sketch042
  Type = 0
FEATURE [Sketcher::SketchObject] Sketch043
  ExternalGeometry = -> [Pad016]
  MapMode = 5
  Placement = pos=(0,0,20) rot=(0,0,1;0rad)
  Support = -> [Pad016]
  sketch-geometry (1):
    g0: Circle CenterX=1.5 CenterY=3 CenterZ=0 NormalX=0 NormalY=0 NormalZ=1 AngleXU=0 Radius=3.1
  constraints (2):
    c: Coincident(g0,g-3)
    c: Radius(g0) = 3.1
FEATURE [PartDesign::Pocket] Pocket016
  BaseFeature = -> Pad016
  Length = 3
  Length2 = 100
  Profile = -> Sketch043
  Type = 0
FEATURE [Sketcher::SketchObject] Sketch044
  ExternalGeometry = -> [Pocket016]
  MapMode = 5
  Placement = pos=(0,14,0) rot=(0,0.707107,0.707107;3.14159rad)
  Support = -> [Pocket016]
  sketch-geometry (10):
    g0: LineSegment StartX=-4 StartY=20 StartZ=0 EndX=-1.5 EndY=20 EndZ=0
    g1: LineSegment StartX=-4 StartY=20 StartZ=0 EndX=-4 EndY=9 EndZ=0
    g2: LineSegment StartX=-1.5 StartY=20 StartZ=0 EndX=-1.5 EndY=9 EndZ=0
    g3: LineSegment StartX=-1.5 StartY=9 StartZ=0 EndX=1.5 EndY=9 EndZ=0
    g4: LineSegment StartX=-4 StartY=9 StartZ=0 EndX=-6.9 EndY=9 EndZ=0
    g5: LineSegment StartX=-6.9 StartY=0 StartZ=0 EndX=-6.9 EndY=9 EndZ=0
    g6: LineSegment StartX=-4.9 StartY=0 StartZ=0 EndX=-4.9 EndY=7 EndZ=0
    g7: LineSegment StartX=-4.9 StartY=7 StartZ=0 EndX=1.5 EndY=7 EndZ=0
    g8: LineSegment StartX=-6.9 StartY=0 StartZ=0 EndX=-4.9 EndY=0 EndZ=0
    g9: LineSegment StartX=1.5 StartY=7 StartZ=0 EndX=1.5 EndY=9 EndZ=0
  constraints (29):
    c: PointOnObject(g0,g-3)
    c: PointOnObject(g0,g-3)
    c: Coincident(g1,g0)
    c: Vertical(g1)
    c: Coincident(g2,g0)
    c: Vertical(g2)
    c: Coincident(g3,g2)
    c: PointOnObject(g3,g-5)
    c: Coincident(g4,g1)
    c: PointOnObject(g4,g-4)
    c: Horizontal(g4)
    c: Coincident(g5,g4)
    c: Coincident(g5,g-4)
    c: Coincident(g6,g7)
    c: Horizontal(g7)
    c: Vertical(g6)
    c: DistanceX(g5,g6) = 2
    c: DistanceY(g-5,g7) = 7
    c: DistanceY(g7,g3) = 2
    c: Horizontal(g3)
    c: DistanceY(g6,g1) = 2
    c: Coincident(g8,g5)
    c: Coincident(g8,g6)
    c: Horizontal(g8)
    c: Coincident(g9,g7)
    c: Coincident(g9,g3)
    c: Vertical(g9)
    c: DistanceX(g0,g0) = 2.5
    c: DistanceX(g0,g-5) = 3
FEATURE [PartDesign::Pocket] Pocket017
  BaseFeature = -> Pocket016
  Length = 7
  Length2 = 100
  Profile = -> Sketch044
  Type = 0
FEATURE [PartDesign::Chamfer] Chamfer010
  Base = -> Pocket017 [Edge59,Edge57]
  BaseFeature = -> Pocket017
  Size = 2.4
FEATURE [PartDesign::Chamfer] Chamfer011
  Base = -> Chamfer010 [Edge48]
  BaseFeature = -> Chamfer010
  Size = 2
FEATURE [PartDesign::Chamfer] Chamfer012
  Base = -> Pocket015 [Edge140]
  BaseFeature = -> Pocket015
  Placement = pos=(0,0,0) rot=(1,0,0;1.5708rad)
  Size = 2
FEATURE [Sketcher::SketchObject] Sketch045
  ExternalGeometry = -> [Chamfer012]
  MapMode = 5
  Placement = pos=(0,8,8.278e-13) rot=(-1,0,0;1.5708rad)
  Support = -> [Chamfer012]
  sketch-geometry (6):
    g0: LineSegment StartX=12.5 StartY=0 StartZ=0 EndX=21 EndY=0 EndZ=0
    g1: LineSegment StartX=12.5 StartY=-18 StartZ=0 EndX=12.5 EndY=0 EndZ=0
    g2: LineSegment StartX=12.5 StartY=-18 StartZ=0 EndX=18.5 EndY=-18 EndZ=0
    g3: LineSegment StartX=18.5 StartY=-18 StartZ=0 EndX=18.5 EndY=-12 EndZ=0
    g4: LineSegment StartX=18.5 StartY=-12 StartZ=0 EndX=21 EndY=-10.6972 EndZ=0
    g5: LineSegment StartX=21 StartY=-10.6972 StartZ=0 EndX=21 EndY=0 EndZ=0
  constraints (14):
    c: Coincident(g1,g0)
    c: Horizontal(g0)
    c: Vertical(g1)
    c: Coincident(g0,g-4)
    c: Coincident(g2,g1)
    c: Coincident(g2,g-6)
    c: Horizontal(g2)
    c: Coincident(g3,g2)
    c: Coincident(g3,g-6)
    c: Coincident(g4,g3)
    c: Coincident(g5,g4)
    c: Coincident(g5,g0)
    c: Vertical(g5)
    c: Coincident(g4,g-7)
FEATURE [PartDesign::Pad] Pad017
  BaseFeature = -> Chamfer012
  Length = 1
  Length2 = 100
  Placement = pos=(0,0,0) rot=(1,0,0;1.5708rad)
  Profile = -> Sketch045
  Reversed = true
  Type = 0
FEATURE [Sketcher::SketchObject] Sketch046
  ExternalGeometry = -> [Chamfer011]
  MapMode = 5
  Placement = pos=(0,14,0) rot=(0,0.707107,0.707107;3.14159rad)
  Support = -> [Chamfer011]
  sketch-geometry (6):
    g0: LineSegment StartX=-7 StartY=20 StartZ=0 EndX=1.4 EndY=20 EndZ=0
    g1: LineSegment StartX=1.4 StartY=0 StartZ=0 EndX=1.4 EndY=20 EndZ=0
    g2: LineSegment StartX=1.4 StartY=0 StartZ=0 EndX=-5 EndY=0 EndZ=0
    g3: LineSegment StartX=-5 StartY=0 StartZ=0 EndX=-5 EndY=7 EndZ=0
    g4: LineSegment StartX=-5 StartY=7 StartZ=0 EndX=-7 EndY=9 EndZ=0
    g5: LineSegment StartX=-7 StartY=9 StartZ=0 EndX=-7 EndY=20 EndZ=0
  constraints (14):
    c: Coincident(g0,g-4)
    c: Coincident(g0,g-6)
    c: Coincident(g1,g-3)
    c: Coincident(g1,g0)
    c: Coincident(g2,g1)
    c: Horizontal(g2)
    c: Vertical(g3)
    c: Coincident(g4,g3)
    c: Coincident(g4,g-4)
    c: Coincident(g5,g4)
    c: Coincident(g5,g0)
    c: Coincident(g3,g-5)
    c: Coincident(g3,g-5)
    c: Coincident(g3,g2)
FEATURE [PartDesign::Pad] Pad018
  BaseFeature = -> Chamfer011
  Length = 1
  Length2 = 100
  Profile = -> Sketch046
  Reversed = true
  Type = 0
FEATURE [PartDesign::Body] Body008  label="slide"
  Group = -> [Sketch042,Pad016,Sketch043,Pocket016,Sketch044,Pocket017,Chamfer010,Chamfer011,Sketch046,Pad018]
  Origin = -> Origin008
  Placement = pos=(0,21.5,38) rot=(0,0,1;0rad)
  Tip = -> Pad018
FEATURE [Sketcher::SketchObject] Sketch047
  ExternalGeometry = -> [Pad017]
  MapMode = 5
  Placement = pos=(0,8,8.278e-13) rot=(-1,0,0;1.5708rad)
  Support = -> [Pad017]
  sketch-geometry (9):
    g0: LineSegment StartX=2 StartY=-2 StartZ=0 EndX=4.3 EndY=-2 EndZ=0
    g1: LineSegment StartX=4.3 StartY=-2 StartZ=0 EndX=4.3 EndY=-8 EndZ=0
    g2: LineSegment StartX=4.3 StartY=-8 StartZ=0 EndX=2 EndY=-8 EndZ=0
    g3: LineSegment StartX=2 StartY=-8 StartZ=0 EndX=2 EndY=-2 EndZ=0
    g4: LineSegment StartX=23.7 StartY=-2 StartZ=0 EndX=26 EndY=-2 EndZ=0
    g5: LineSegment StartX=26 StartY=-2 StartZ=0 EndX=26 EndY=-8 EndZ=0
    g6: LineSegment StartX=26 StartY=-8 StartZ=0 EndX=23.7 EndY=-8 EndZ=0
    g7: LineSegment StartX=23.7 StartY=-8 StartZ=0 EndX=23.7 EndY=-2 EndZ=0
    g8: LineSegment [constr] StartX=28 StartY=-5 StartZ=0 EndX=0 EndY=-5 EndZ=0
  constraints (27):
    c: Coincident(g0,g1)
    c: Coincident(g1,g2)
    c: Coincident(g2,g3)
    c: Coincident(g3,g0)
    c: Horizontal(g0)
    c: Horizontal(g2)
    c: Vertical(g1)
    c: Vertical(g3)
    c: Coincident(g4,g5)
    c: Coincident(g5,g6)
    c: Coincident(g6,g7)
    c: Coincident(g7,g4)
    c: Horizontal(g4)
    c: Horizontal(g6)
    c: Vertical(g5)
    c: Vertical(g7)
    c: Coincident(g8,g-3)
    c: PointOnObject(g8,g-2)
    c: Horizontal(g8)
    c: DistanceX(g0,g0) = 2.3
    c: Equal(g6,g2)
    c: DistanceY(g1,g1) = 6
    c: Equal(g1,g5)
    c: Symmetric(g1,g0,g8)
    c: Symmetric(g5,g4,g8)
    c: DistanceX(g8,g2) = 2
    c: DistanceX(g5,g8) = 2
FEATURE [PartDesign::Pocket] Pocket018
  BaseFeature = -> Pad017
  Length = 9
  Length2 = 100
  Placement = pos=(0,0,0) rot=(1,0,0;1.5708rad)
  Profile = -> Sketch047
  Type = 0
FEATURE [PartDesign::Body] Body007  label="carriage_belt_holder001"
  Group = -> [Sketch021,Pad010,Sketch022,Pad011,Sketch032,Pocket010,Sketch033,Pocket011,Sketch034,Pocket012,Sketch035,Sketch036,Pad012,Pad013,Sketch037,Pocket013,Sketch038,Pocket014,Chamfer005,Chamfer006,Chamfer007,Sketch039,Pad014,Sketch040,Pad015,Chamfer008,Sketch041,Pocket015,Chamfer012,Sketch045,Pad017,Sketch047,Pocket018]
  Origin = -> Origin007
  Placement = pos=(-14,27.5,3) rot=(0,0,1;0rad)
  Tip = -> Pocket018
FEATURE [Sketcher::SketchObject] Sketch048
  MapMode = 5
  Placement = pos=(0,0,0) rot=(1,0,0;1.5708rad)
  Support = -> [XZ_Plane009]
  sketch-geometry (12):
    g0: LineSegment StartX=-14 StartY=0 StartZ=0 EndX=14 EndY=0 EndZ=0
    g1: LineSegment StartX=14 StartY=0 StartZ=0 EndX=14 EndY=45 EndZ=0
    g2: LineSegment StartX=14 StartY=45 StartZ=0 EndX=-14 EndY=45 EndZ=0
    g3: LineSegment StartX=-14 StartY=45 StartZ=0 EndX=-14 EndY=0 EndZ=0
    g4: LineSegment [constr] StartX=-10 StartY=32.5 StartZ=0 EndX=10 EndY=32.5 EndZ=0
    g5: LineSegment [constr] StartX=10 StartY=32.5 StartZ=0 EndX=10 EndY=12.5 EndZ=0
    g6: LineSegment [constr] StartX=10 StartY=12.5 StartZ=0 EndX=-10 EndY=12.5 EndZ=0
    g7: LineSegment [constr] StartX=-10 StartY=12.5 StartZ=0 EndX=-10 EndY=32.5 EndZ=0
    g8: Circle CenterX=-10 CenterY=32.5 CenterZ=0 NormalX=0 NormalY=0 NormalZ=1 AngleXU=0 Radius=1.6
    g9: Circle CenterX=10 CenterY=32.5 CenterZ=0 NormalX=0 NormalY=0 NormalZ=1 AngleXU=0 Radius=1.6
    g10: Circle CenterX=-10 CenterY=12.5 CenterZ=0 NormalX=0 NormalY=0 NormalZ=1 AngleXU=0 Radius=1.6
    g11: Circle CenterX=10 CenterY=12.5 CenterZ=0 NormalX=0 NormalY=0 NormalZ=1 AngleXU=0 Radius=1.6
  constraints (32):
    c: Coincident(g0,g1)
    c: Coincident(g1,g2)
    c: Coincident(g2,g3)
    c: Coincident(g3,g0)
    c: Horizontal(g0)
    c: Horizontal(g2)
    c: Vertical(g1)
    c: Vertical(g3)
    c: Symmetric(g0,g0,g-2)
    c: DistanceX(g0,g0) = 28
    c: DistanceY(g1,g1) = 45
    c: Coincident(g4,g5)
    c: Coincident(g5,g6)
    c: Coincident(g6,g7)
    c: Coincident(g7,g4)
    c: Horizontal(g4)
    c: Horizontal(g6)
    c: Vertical(g5)
    c: Vertical(g7)
    c: Coincident(g8,g4)
    c: Coincident(g9,g4)
    c: Coincident(g10,g6)
    c: Coincident(g11,g5)
    c: Radius(g11) = 1.6
    c: Equal(g11,g9)
    c: Equal(g11,g8)
    c: Equal(g11,g10)
    c: DistanceY(g7,g7) = 20
    c: DistanceX(g4,g4) = 20
    c: DistanceY(g0,g6) = 12.5
    c: Symmetric(g5,g6,g-2)
    c: PointOnObject(g0,g-1)
FEATURE [PartDesign::Pad] Pad019
  Length = 2.5
  Length2 = 100
  Placement = pos=(0,0,0) rot=(1,0,0;1.5708rad)
  Profile = -> Sketch048
  Type = 0
FEATURE [PartDesign::Body] Body009  label="separator"
  Group = -> [Sketch048,Pad019]
  Origin = -> Origin009
  Placement = pos=(0,21.5,3.08) rot=(0,0,1;0rad)
  Tip = -> Pad019
FEATURE [Sketcher::SketchObject] Sketch050
  MapMode = 5
  Placement = pos=(0,0,0) rot=(1,0,0;1.5708rad)
  Support = -> [XZ_Plane010]
  sketch-geometry (8):
    g0: LineSegment StartX=-29 StartY=48 StartZ=0 EndX=27 EndY=48 EndZ=0
    g1: LineSegment StartX=27 StartY=48 StartZ=0 EndX=27 EndY=3 EndZ=0
    g2: LineSegment StartX=27 StartY=3 StartZ=0 EndX=-29 EndY=3 EndZ=0
    g3: LineSegment StartX=-29 StartY=3 StartZ=0 EndX=-29 EndY=48 EndZ=0
    g4: Circle CenterX=20.3 CenterY=10 CenterZ=0 NormalX=0 NormalY=0 NormalZ=1 AngleXU=0 Radius=2.5
    g5: Circle CenterX=20.3 CenterY=41 CenterZ=0 NormalX=0 NormalY=0 NormalZ=1 AngleXU=0 Radius=2.5
    g6: Circle CenterX=-20.3 CenterY=25.5 CenterZ=0 NormalX=0 NormalY=0 NormalZ=1 AngleXU=0 Radius=3.6
    g7: LineSegment [constr] StartX=-20.3 StartY=25.5 StartZ=0 EndX=0 EndY=25.5 EndZ=0
  constraints (24):
    c: Coincident(g0,g1)
    c: Coincident(g1,g2)
    c: Coincident(g2,g3)
    c: Coincident(g3,g0)
    c: Horizontal(g0)
    c: Horizontal(g2)
    c: Vertical(g1)
    c: Vertical(g3)
    c: DistanceX(g2,g2) = 56
    c: DistanceY(g1,g1) = 45
    c: Radius(g5) = 2.5
    c: Equal(g5,g4)
    c: DistanceX(g5,g0) = 6.7
    c: DistanceY(g5,g0) = 7
    c: DistanceY(g1,g4) = 7
    c: DistanceX(g4,g1) = 6.7
    c: DistanceY(g-1,g1) = 3
    c: DistanceX(g0,g6) = 8.7
    c: Coincident(g7,g6)
    c: PointOnObject(g7,g-2)
    c: Horizontal(g7)
    c: Symmetric(g2,g0,g7)
    c: Radius(g6) = 3.6
    c: DistanceX(g-1,g1) = 27
FEATURE [PartDesign::Pad] Pad021
  Length = 5
  Length2 = 100
  Placement = pos=(0,0,0) rot=(1,0,0;1.5708rad)
  Profile = -> Sketch050
  Type = 0
FEATURE [PartDesign::Fillet] Fillet004
  Base = -> Pad021 [Edge2,Edge5,Edge8,Edge1]
  BaseFeature = -> Pad021
  Placement = pos=(0,0,0) rot=(1,0,0;1.5708rad)
  Radius = 5
FEATURE [Sketcher::SketchObject] Sketch049
  ExternalGeometry = -> [Fillet004]
  MapMode = 5
  Placement = pos=(0,-1e-16,0) rot=(-1,0,0;1.5708rad)
  Support = -> [Fillet004]
  sketch-geometry (33):
    g0: LineSegment [constr] StartX=-10 StartY=-15.5 StartZ=0 EndX=10 EndY=-15.5 EndZ=0
    g1: LineSegment [constr] StartX=10 StartY=-15.5 StartZ=0 EndX=10 EndY=-35.5 EndZ=0
    g2: LineSegment [constr] StartX=10.7745 StartY=-35.5 StartZ=0 EndX=-10 EndY=-35.5 EndZ=0
    g3: LineSegment [constr] StartX=-10 StartY=-35.5 StartZ=0 EndX=-10 EndY=-15.5 EndZ=0
    g4: LineSegment StartX=-7.14212 StartY=-17.15 StartZ=0 EndX=-7.14212 EndY=-13.85 EndZ=0
    g5: LineSegment StartX=-7.14212 StartY=-13.85 StartZ=0 EndX=-10 EndY=-12.2 EndZ=0
    g6: LineSegment StartX=-10 StartY=-12.2 StartZ=0 EndX=-12.8579 EndY=-13.85 EndZ=0
    g7: LineSegment StartX=-12.8579 StartY=-13.85 StartZ=0 EndX=-12.8579 EndY=-17.15 EndZ=0
    g8: LineSegment StartX=-12.8579 StartY=-17.15 StartZ=0 EndX=-10 EndY=-18.8 EndZ=0
    g9: LineSegment StartX=-10 StartY=-18.8 StartZ=0 EndX=-7.14212 EndY=-17.15 EndZ=0
    g10: Circle [constr] CenterX=-10 CenterY=-15.5 CenterZ=0 NormalX=0 NormalY=0 NormalZ=1 AngleXU=0 Radius=3.3
    g11: LineSegment StartX=-7.14212 StartY=-33.85 StartZ=0 EndX=-10 EndY=-32.2 EndZ=0
    g12: LineSegment StartX=-10 StartY=-32.2 StartZ=0 EndX=-12.8579 EndY=-33.85 EndZ=0
    g13: LineSegment StartX=-12.8579 StartY=-33.85 StartZ=0 EndX=-12.8579 EndY=-37.15 EndZ=0
    g14: LineSegment StartX=-12.8579 StartY=-37.15 StartZ=0 EndX=-10 EndY=-38.8 EndZ=0
    g15: LineSegment StartX=-10 StartY=-38.8 StartZ=0 EndX=-7.14212 EndY=-37.15 EndZ=0
    g16: LineSegment StartX=-7.14212 StartY=-37.15 StartZ=0 EndX=-7.14212 EndY=-33.85 EndZ=0
    g17: Circle [constr] CenterX=-10 CenterY=-35.5 CenterZ=0 NormalX=0 NormalY=0 NormalZ=1 AngleXU=0 Radius=3.3
    g18: LineSegment StartX=12.8579 StartY=-37.15 StartZ=0 EndX=12.8579 EndY=-33.85 EndZ=0
    g19: LineSegment StartX=12.8579 StartY=-33.85 StartZ=0 EndX=10 EndY=-32.2 EndZ=0
    g20: LineSegment StartX=10 StartY=-32.2 StartZ=0 EndX=7.14212 EndY=-33.85 EndZ=0
    g21: LineSegment StartX=7.14212 StartY=-33.85 StartZ=0 EndX=7.14212 EndY=-37.15 EndZ=0
    g22: LineSegment StartX=7.14212 StartY=-37.15 StartZ=0 EndX=10 EndY=-38.8 EndZ=0
    g23: LineSegment StartX=10 StartY=-38.8 StartZ=0 EndX=12.8579 EndY=-37.15 EndZ=0
    g24: Circle [constr] CenterX=10 CenterY=-35.5 CenterZ=0 NormalX=0 NormalY=0 NormalZ=1 AngleXU=0 Radius=3.3
    g25: LineSegment StartX=12.8579 StartY=-17.15 StartZ=0 EndX=12.8579 EndY=-13.85 EndZ=0
    g26: LineSegment StartX=12.8579 StartY=-13.85 StartZ=0 EndX=10 EndY=-12.2 EndZ=0
    g27: LineSegment StartX=10 StartY=-12.2 StartZ=0 EndX=7.14212 EndY=-13.85 EndZ=0
    g28: LineSegment StartX=7.14212 StartY=-13.85 StartZ=0 EndX=7.14212 EndY=-17.15 EndZ=0
    g29: LineSegment StartX=7.14212 StartY=-17.15 StartZ=0 EndX=10 EndY=-18.8 EndZ=0
    g30: LineSegment StartX=10 StartY=-18.8 StartZ=0 EndX=12.8579 EndY=-17.15 EndZ=0
    g31: Circle [constr] CenterX=10 CenterY=-15.5 CenterZ=0 NormalX=0 NormalY=0 NormalZ=1 AngleXU=0 Radius=3.3
    g32: LineSegment [constr] StartX=-29 StartY=-25.5 StartZ=0 EndX=10 EndY=-25.5 EndZ=0
  constraints (78):
    c: Coincident(g0,g1)
    c: Coincident(g2,g3)
    c: Coincident(g3,g0)
    c: Horizontal(g0)
    c: Horizontal(g2)
    c: Vertical(g1)
    c: Vertical(g3)
    c: DistanceX(g0,g0) = 20
    c: DistanceY(g1,g1) = 20
    c: Symmetric(g2,g1,g-2)
    c: Coincident(g4,g5)
    c: Coincident(g5,g6)
    c: Coincident(g6,g7)
    c: Coincident(g7,g8)
    c: Coincident(g8,g9)
    c: Coincident(g9,g4)
    c: Equal(g4, g5-g9) x5
    c: PointOnObject(g4,g10)
    c: PointOnObject(g5,g10)
    c: PointOnObject(g6,g10)
    c: PointOnObject(g7,g10)
    c: PointOnObject(g8,g10)
    c: PointOnObject(g9,g10)
    c: Coincident(g10,g0)
    c: Coincident(g11,g12)
    c: Coincident(g12,g13)
    c: Coincident(g13,g14)
    c: Coincident(g14,g15)
    c: Coincident(g15,g16)
    c: Coincident(g16,g11)
    c: Equal(g11, g12-g16) x5
    c: PointOnObject(g11,g17)
    c: PointOnObject(g12,g17)
    c: PointOnObject(g13,g17)
    c: PointOnObject(g14,g17)
    c: PointOnObject(g15,g17)
    c: PointOnObject(g16,g17)
    c: Coincident(g17,g2)
    c: Coincident(g18,g19)
    c: Coincident(g19,g20)
    c: Coincident(g20,g21)
    c: Coincident(g21,g22)
    c: Coincident(g22,g23)
    c: Coincident(g23,g18)
    c: Equal(g18, g19-g23) x5
    c: PointOnObject(g18,g24)
    c: PointOnObject(g19,g24)
    c: PointOnObject(g20,g24)
    c: PointOnObject(g21,g24)
    c: PointOnObject(g22,g24)
    c: PointOnObject(g23,g24)
    c: Coincident(g25,g26)
    c: Coincident(g26,g27)
    c: Coincident(g27,g28)
    c: Coincident(g28,g29)
    c: Coincident(g29,g30)
    c: Coincident(g30,g25)
    c: Equal(g25, g26-g30) x5
    c: PointOnObject(g25,g31)
    c: PointOnObject(g26,g31)
    c: PointOnObject(g27,g31)
    c: PointOnObject(g28,g31)
    c: PointOnObject(g29,g31)
    c: PointOnObject(g30,g31)
    c: Coincident(g31,g0)
    c: Vertical(g7)
    c: Vertical(g13)
    c: Vertical(g28)
    c: Vertical(g21)
    c: Radius(g31) = 3.3
    c: Equal(g31,g10)
    c: Equal(g31,g17)
    c: Equal(g31,g24)
    c: PointOnObject(g32,g1)
    c: Coincident(g24,g1)
    c: Symmetric(g1,g0,g32)
    c: PointOnObject(g32,g-4)
    c: Symmetric(g-4,g-4,g32)
FEATURE [PartDesign::Pocket] Pocket019
  BaseFeature = -> Fillet004
  Length = 5
  Length2 = 100
  Placement = pos=(0,0,0) rot=(1,0,0;1.5708rad)
  Profile = -> Sketch049
  Type = 0
FEATURE [Sketcher::SketchObject] Sketch051
  ExternalGeometry = -> [Pocket019]
  MapMode = 5
  Placement = pos=(0,-1e-16,0) rot=(-1,0,0;1.5708rad)
  Support = -> [Pocket019]
  sketch-geometry (24):
    g0: LineSegment [constr] StartX=7.14212 StartY=-17.15 StartZ=0 EndX=12.8579 EndY=-13.85 EndZ=0
    g1: LineSegment [constr] StartX=10 StartY=-18.8 StartZ=0 EndX=10 EndY=-15.5 EndZ=0
    g2: LineSegment [constr] StartX=7.14212 StartY=-37.15 StartZ=0 EndX=12.8579 EndY=-33.85 EndZ=0
    g3: LineSegment [constr] StartX=10 StartY=-38.8 StartZ=0 EndX=10 EndY=-35.5 EndZ=0
    g4: LineSegment [constr] StartX=-12.8579 StartY=-37.15 StartZ=0 EndX=-7.14212 EndY=-33.85 EndZ=0
    g5: LineSegment [constr] StartX=-10 StartY=-38.8 StartZ=0 EndX=-10 EndY=-35.5 EndZ=0
    g6: LineSegment [constr] StartX=-12.8579 StartY=-13.85 StartZ=0 EndX=-7.14212 EndY=-17.15 EndZ=0
    g7: LineSegment [constr] StartX=-10 StartY=-18.8 StartZ=0 EndX=-10 EndY=-15.5 EndZ=0
    g8: ArcOfCircle CenterX=20.3 CenterY=-10 CenterZ=0 NormalX=0 NormalY=0 NormalZ=1 AngleXU=0 Radius=8 StartAngle=2.72015 EndAngle=4.67488
    g9: ArcOfCircle CenterX=20.3 CenterY=-41 CenterZ=0 NormalX=0 NormalY=0 NormalZ=1 AngleXU=0 Radius=8 StartAngle=1.60831 EndAngle=3.56303
    g10: ArcOfCircle CenterX=-20.3 CenterY=-25.5 CenterZ=0 NormalX=0 NormalY=0 NormalZ=1 AngleXU=0 Radius=9 StartAngle=5.08781 EndAngle=7.47856
    g11: LineSegment StartX=-17 StartY=-17.1268 StartZ=0 EndX=-17 EndY=-3 EndZ=0
    g12: LineSegment StartX=-17 StartY=-3 StartZ=0 EndX=13 EndY=-3 EndZ=0
    g13: LineSegment StartX=13 StartY=-6.72739 StartZ=0 EndX=13 EndY=-3 EndZ=0
    g14: LineSegment StartX=20 StartY=-17.9944 StartZ=0 EndX=27 EndY=-17.9944 EndZ=0
    g15: LineSegment StartX=27 StartY=-17.9944 StartZ=0 EndX=27 EndY=-33.0056 EndZ=0
    g16: LineSegment StartX=20 StartY=-33.0056 StartZ=0 EndX=27 EndY=-33.0056 EndZ=0
    g17: LineSegment StartX=13 StartY=-44.2726 StartZ=0 EndX=13 EndY=-48 EndZ=0
    g18: LineSegment StartX=-17 StartY=-33.8732 StartZ=0 EndX=-17 EndY=-48 EndZ=0
    g19: LineSegment StartX=-17 StartY=-48 StartZ=0 EndX=13 EndY=-48 EndZ=0
    g20: Circle CenterX=-10 CenterY=-15.5 CenterZ=0 NormalX=0 NormalY=0 NormalZ=1 AngleXU=0 Radius=1.6
    g21: Circle CenterX=10 CenterY=-15.5 CenterZ=0 NormalX=0 NormalY=0 NormalZ=1 AngleXU=0 Radius=1.6
    g22: Circle CenterX=10 CenterY=-35.5 CenterZ=0 NormalX=0 NormalY=0 NormalZ=1 AngleXU=0 Radius=1.6
    g23: Circle CenterX=-10 CenterY=-35.5 CenterZ=0 NormalX=0 NormalY=0 NormalZ=1 AngleXU=0 Radius=1.6
  constraints (64):
    c: Coincident(g0,g-13)
    c: Coincident(g0,g-14)
    c: Coincident(g1,g-13)
    c: Vertical(g1)
    c: PointOnObject(g1,g0)
    c: Coincident(g2,g-11)
    c: Coincident(g2,g-12)
    c: Coincident(g3,g-11)
    c: PointOnObject(g3,g2)
    c: Coincident(g4,g-10)
    c: Coincident(g4,g-9)
    c: Coincident(g5,g-10)
    c: PointOnObject(g5,g4)
    c: Coincident(g6,g-8)
    c: Coincident(g6,g-7)
    c: Coincident(g7,g-7)
    c: PointOnObject(g7,g6)
    c: Vertical(g5)
    c: Vertical(g7)
    c: Vertical(g3)
    c: Coincident(g8,g-5)
    c: Coincident(g9,g-4)
    c: Coincident(g10,g-6)
    c: Coincident(g11,g10)
    c: Vertical(g11)
    c: Coincident(g12,g11)
    c: Horizontal(g12)
    c: Coincident(g13,g8)
    c: Coincident(g13,g12)
    c: Coincident(g14,g8)
    c: Horizontal(g14)
    c: Coincident(g15,g14)
    c: Vertical(g15)
    c: Coincident(g16,g9)
    c: Coincident(g16,g15)
    c: Horizontal(g16)
    c: Coincident(g17,g9)
    c: PointOnObject(g17,g-15)
    c: Coincident(g18,g10)
    c: PointOnObject(g18,g-15)
    c: Vertical(g18)
    c: Coincident(g19,g18)
    c: Coincident(g19,g17)
    c: PointOnObject(g12,g-16)
    c: Vertical(g13)
    c: Vertical(g17)
    c: Radius(g9) = 8
    c: Equal(g9,g8)
    c: Radius(g10) = 9
    c: Equal(g19,g12)
    c: DistanceX(g19,g19) = 30
    c: DistanceX(g-1,g12) = 13
    c: DistanceX(g-1,g17) = 13
    c: PointOnObject(g15,g-3)
    c: Coincident(g20,g7)
    c: Coincident(g21,g1)
    c: Coincident(g22,g3)
    c: Coincident(g23,g5)
    c: Radius(g21) = 1.6
    c: Equal(g21,g20)
    c: Equal(g21,g22)
    c: Equal(g21,g23)
    c: Equal(g14,g16)
    c: DistanceX(g14,g14) = 7
FEATURE [PartDesign::Pad] Pad022
  BaseFeature = -> Pocket019
  Length = 6
  Length2 = 100
  Placement = pos=(0,0,0) rot=(1,0,0;1.5708rad)
  Profile = -> Sketch051
  Type = 0
FEATURE [PartDesign::Chamfer] Chamfer013
  Base = -> Pad022 [Edge13,Edge11,Edge78]
  BaseFeature = -> Pad022
  Placement = pos=(0,0,0) rot=(1,0,0;1.5708rad)
  Size = 5.9999
FEATURE [PartDesign::Body] Body010  label="carriage_v2"
  Group = -> [Sketch050,Pad021,Fillet004,Sketch049,Pocket019,Sketch051,Pad022,Chamfer013]
  Origin = -> Origin010
  Placement = pos=(0,16.5,0) rot=(0,0,1;0rad)
  Tip = -> Chamfer013
